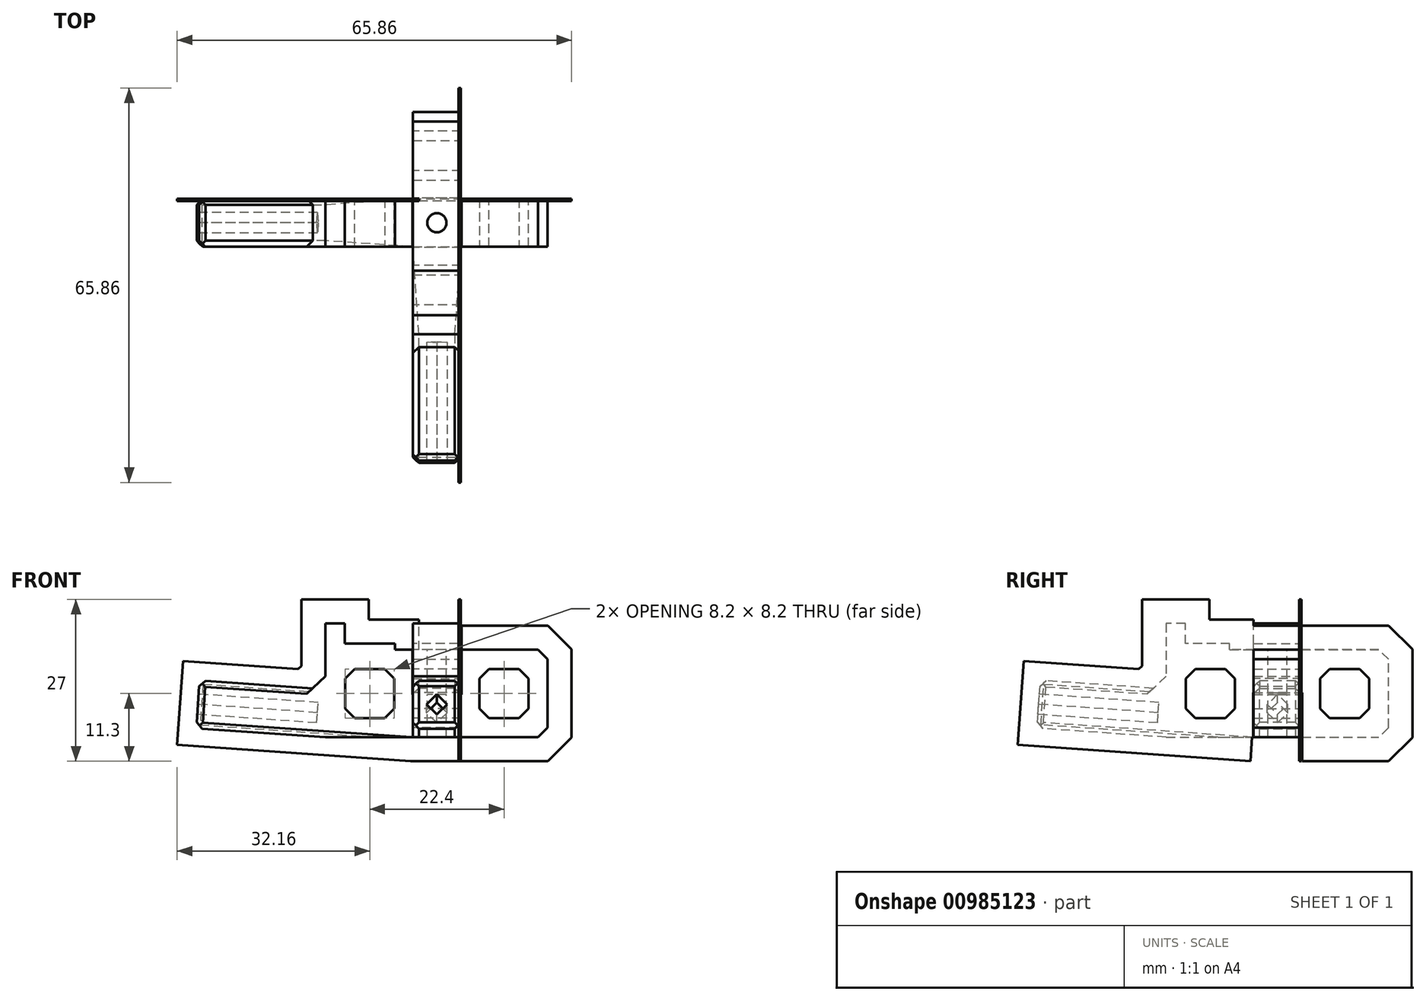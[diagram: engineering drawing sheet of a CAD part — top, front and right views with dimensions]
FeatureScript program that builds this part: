
annotation { "Feature Type Name" : "Feature", "Feature Type Description" : "" }
export const myFeature = defineFeature(function(context is Context, id is Id, definition is map)
    precondition{}
    {
        {
            var Q0;
            Q0=qCreatedBy(makeId("Top.planeOp"),FACE);
            var sketch = newSketch(context, id + "F0", { "sketchPlane" : qUnion([Q0])});
            skLineSegment(sketch, "E0.bottom", {"start": v(0, 0) * mm, "end": v(-5, 0) * mm, "construction": true});
            skLineSegment(sketch, "E0.top", {"start": v(0, -5) * mm, "end": v(-5, -5) * mm, "construction": true});
            skLineSegment(sketch, "E0.left", {"start": v(0, 0) * mm, "end": v(0, -5) * mm, "construction": true});
            skLineSegment(sketch, "E0.right", {"start": v(-5, 0) * mm, "end": v(-5, -5) * mm, "construction": true});
            skLineSegment(sketch, "E1.bottom", {"start": v(0, 0) * mm, "end": v(-15, 0) * mm, "construction": true});
            skLineSegment(sketch, "E1.top", {"start": v(0, -15) * mm, "end": v(-15, -15) * mm, "construction": true});
            skLineSegment(sketch, "E1.left", {"start": v(0, 0) * mm, "end": v(0, -15) * mm, "construction": true});
            skLineSegment(sketch, "E1.right", {"start": v(-15, 0) * mm, "end": v(-15, -15) * mm, "construction": true});
            skCircle(sketch, "E2", {"center": v(0, 0) * mm, "radius": 1.6 * mm, "construction": true});
            skLineSegment(sketch, "E3.bottom", {"start": v(0, 0) * mm, "end": v(-57.4, 0) * mm, "construction": true});
            skLineSegment(sketch, "E3.top", {"start": v(0, -32) * mm, "end": v(-57.4, -32) * mm, "construction": true});
            skLineSegment(sketch, "E3.left", {"start": v(0, 0) * mm, "end": v(0, -32) * mm, "construction": true});
            skLineSegment(sketch, "E3.right", {"start": v(-57.4, 0) * mm, "end": v(-57.4, -32) * mm, "construction": true});
            skSolve(sketch);
        }
        {
            var Q0;
            Q0=qCreatedBy(makeId("Front.planeOp"),FACE);
            var sketch = newSketch(context, id + "F1", { "sketchPlane" : qUnion([Q0])});
            skPoint(sketch, "E4.0", {"position": v(0, 0) * mm});
            skPoint(sketch, "E4.1", {"position": v(-5, 0) * mm});
            skPoint(sketch, "E4.2", {"position": v(-15, 0) * mm});
            skPoint(sketch, "E4.3", {"position": v(-57.4, 0) * mm});
            skLineSegment(sketch, "E5.bottom", {"start": v(0, 0) * mm, "end": v(-57.4, 0) * mm, "construction": true});
            skLineSegment(sketch, "E5.top", {"start": v(0, -2.2) * mm, "end": v(-57.4, -2.2) * mm, "construction": true});
            skLineSegment(sketch, "E5.left", {"start": v(0, 0) * mm, "end": v(0, -2.2) * mm, "construction": true});
            skLineSegment(sketch, "E5.right", {"start": v(-57.4, 0) * mm, "end": v(-57.4, -2.2) * mm, "construction": true});
            skLineSegment(sketch, "E6.bottom", {"start": v(-15, 0) * mm, "end": v(0, 0) * mm, "construction": true});
            skLineSegment(sketch, "E6.top", {"start": v(-15, -8.2) * mm, "end": v(0, -8.2) * mm, "construction": true});
            skLineSegment(sketch, "E6.left", {"start": v(-15, 0) * mm, "end": v(-15, -8.2) * mm, "construction": true});
            skLineSegment(sketch, "E6.right", {"start": v(0, 0) * mm, "end": v(0, -8.2) * mm, "construction": true});
            skLineSegment(sketch, "E7.bottom", {"start": v(-5, 0) * mm, "end": v(0, 0) * mm, "construction": true});
            skLineSegment(sketch, "E7.left", {"start": v(-5, 0) * mm, "end": v(-5, -9.6) * mm, "construction": true});
            skLineSegment(sketch, "E7.right", {"start": v(0, 0) * mm, "end": v(0, -9.6) * mm, "construction": true});
            skLineSegment(sketch, "E8.bottom", {"start": v(-18.6, -9.6) * mm, "end": v(-15.4, -9.6) * mm});
            skLineSegment(sketch, "E8.top", {"start": v(-18.6, -5.2) * mm, "end": v(-15.4, -5.2) * mm});
            skLineSegment(sketch, "E8.left", {"start": v(-18.6, -9.6) * mm, "end": v(-18.6, -5.2) * mm});
            skLineSegment(sketch, "E8.right", {"start": v(-15.4, -9.6) * mm, "end": v(-15.4, -5.2) * mm});
            skLineSegment(sketch, "E9.bottom", {"start": v(0, -24.2) * mm, "end": v(18.5, -24.2) * mm});
            skLineSegment(sketch, "E9.top", {"start": v(0, -9.6) * mm, "end": v(18.5, -9.6) * mm});
            skLineSegment(sketch, "E9.right", {"start": v(18.5, -24.2) * mm, "end": v(18.5, -9.6) * mm});
            skLineSegment(sketch, "E10.left", {"start": v(-18.6, -5.2) * mm, "end": v(-18.6, -11.6) * mm});
            skLineSegment(sketch, "E11.bottom", {"start": v(-15.4, -9.6) * mm, "end": v(-7, -9.6) * mm});
            skLineSegment(sketch, "E11.top", {"start": v(-15.4, -8.6) * mm, "end": v(-7, -8.6) * mm});
            skLineSegment(sketch, "E11.left", {"start": v(-15.4, -9.6) * mm, "end": v(-15.4, -8.6) * mm});
            skLineSegment(sketch, "E11.right", {"start": v(-7, -9.6) * mm, "end": v(-7, -8.6) * mm});
            skLineSegment(sketch, "E12", {"start": v(-18.6, -9.6) * mm, "end": v(-18.6, -24.2) * mm, "construction": true});
            skLineSegment(sketch, "E13", {"start": v(-39.6, -14.71) * mm, "end": v(-18.6, -16.18) * mm});
            skLineSegment(sketch, "E14", {"start": v(-40.16, -22.7) * mm, "end": v(-18.6, -24.2) * mm});
            skLineSegment(sketch, "E15", {"start": v(-39.6, -14.71) * mm, "end": v(-40.16, -22.7) * mm});
            skLineSegment(sketch, "E16", {"start": v(0, -24.2) * mm, "end": v(-18.6, -24.2) * mm});
            skLineSegment(sketch, "E17", {"start": v(-18.6, -9.6) * mm, "end": v(-18.6, -16.18) * mm});
            skLineSegment(sketch, "E18", {"start": v(0, -24.2) * mm, "end": v(0, -9.6) * mm, "construction": true});
            skLineSegment(sketch, "E19", {"start": v(-5, -9.6) * mm, "end": v(0, -9.6) * mm});
            skLineSegment(sketch, "E20", {"start": v(-7, -9.6) * mm, "end": v(-5, -9.6) * mm});
            skLineSegment(sketch, "E21", {"start": v(18.5, -16.9) * mm, "end": v(0, -16.9) * mm, "construction": true});
            skLineSegment(sketch, "E22", {"start": v(0, -16.9) * mm, "end": v(-18.6, -16.9) * mm, "construction": true});
            skLineSegment(sketch, "E23.bottom", {"start": v(-4.1, -9.6) * mm, "end": v(4.1, -9.6) * mm});
            skLineSegment(sketch, "E23.top", {"start": v(-4.1, -17.05) * mm, "end": v(4.1, -17.05) * mm});
            skLineSegment(sketch, "E23.left", {"start": v(-4.1, -9.6) * mm, "end": v(-4.1, -17.05) * mm});
            skLineSegment(sketch, "E23.right", {"start": v(4.1, -9.6) * mm, "end": v(4.1, -17.05) * mm});
            skPoint(sketch, "E23.middle", {"position": v(0, -13.32) * mm});
            skLineSegment(sketch, "E24.bottom", {"start": v(-15.3, -12.8) * mm, "end": v(-7.1, -12.8) * mm});
            skLineSegment(sketch, "E24.top", {"start": v(-15.3, -21) * mm, "end": v(-7.1, -21) * mm});
            skLineSegment(sketch, "E24.left", {"start": v(-15.3, -12.8) * mm, "end": v(-15.3, -21) * mm});
            skLineSegment(sketch, "E24.right", {"start": v(-7.1, -12.8) * mm, "end": v(-7.1, -21) * mm});
            skPoint(sketch, "E24.middle", {"position": v(-11.2, -16.9) * mm});
            skLineSegment(sketch, "E25.bottom", {"start": v(7.1, -12.8) * mm, "end": v(15.3, -12.8) * mm});
            skLineSegment(sketch, "E25.top", {"start": v(7.1, -21) * mm, "end": v(15.3, -21) * mm});
            skLineSegment(sketch, "E25.left", {"start": v(7.1, -12.8) * mm, "end": v(7.1, -21) * mm});
            skLineSegment(sketch, "E25.right", {"start": v(15.3, -12.8) * mm, "end": v(15.3, -21) * mm});
            skPoint(sketch, "E25.middle", {"position": v(11.2, -16.9) * mm});
            skSolve(sketch);
        }
        {
            var Q0;
            Q0=qCreatedBy(makeId("Right.planeOp"),FACE);
            var sketch = newSketch(context, id + "F2", { "sketchPlane" : qUnion([Q0])});
            skPoint(sketch, "E26.0", {"position": v(0, 0) * mm});
            skPoint(sketch, "E26.1", {"position": v(-5, 0) * mm});
            skPoint(sketch, "E26.2", {"position": v(-15, 0) * mm});
            skPoint(sketch, "E26.3", {"position": v(-32, 0) * mm});
            skPoint(sketch, "E27.0", {"position": v(0, -2.2) * mm});
            skPoint(sketch, "E27.1", {"position": v(0, -8.2) * mm});
            skPoint(sketch, "E27.2", {"position": v(0, -9.6) * mm});
            skLineSegment(sketch, "E28.bottom", {"start": v(0, -2.2) * mm, "end": v(-32, -2.2) * mm, "construction": true});
            skLineSegment(sketch, "E28.top", {"start": v(0, 0) * mm, "end": v(-32, 0) * mm, "construction": true});
            skLineSegment(sketch, "E28.left", {"start": v(0, -2.2) * mm, "end": v(0, 0) * mm, "construction": true});
            skLineSegment(sketch, "E28.right", {"start": v(-32, -2.2) * mm, "end": v(-32, 0) * mm, "construction": true});
            skLineSegment(sketch, "E29.bottom", {"start": v(0, -9.6) * mm, "end": v(-5, -9.6) * mm, "construction": true});
            skLineSegment(sketch, "E29.top", {"start": v(0, 0) * mm, "end": v(-5, 0) * mm, "construction": true});
            skLineSegment(sketch, "E29.left", {"start": v(0, -9.6) * mm, "end": v(0, 0) * mm, "construction": true});
            skLineSegment(sketch, "E29.right", {"start": v(-5, -9.6) * mm, "end": v(-5, 0) * mm, "construction": true});
            skLineSegment(sketch, "E30.bottom", {"start": v(0, -8.2) * mm, "end": v(-15, -8.2) * mm, "construction": true});
            skLineSegment(sketch, "E30.top", {"start": v(0, 0) * mm, "end": v(-15, 0) * mm, "construction": true});
            skLineSegment(sketch, "E30.left", {"start": v(0, -8.2) * mm, "end": v(0, 0) * mm, "construction": true});
            skLineSegment(sketch, "E30.right", {"start": v(-15, -8.2) * mm, "end": v(-15, 0) * mm, "construction": true});
            skLineSegment(sketch, "E31.bottom", {"start": v(-15.4, -9.6) * mm, "end": v(-18.6, -9.6) * mm});
            skLineSegment(sketch, "E31.top", {"start": v(-15.4, -5.2) * mm, "end": v(-18.6, -5.2) * mm});
            skLineSegment(sketch, "E31.left", {"start": v(-15.4, -9.6) * mm, "end": v(-15.4, -5.2) * mm});
            skLineSegment(sketch, "E31.right", {"start": v(-18.6, -9.6) * mm, "end": v(-18.6, -5.2) * mm});
            skLineSegment(sketch, "E32.bottom", {"start": v(0, -9.6) * mm, "end": v(18.5, -9.6) * mm});
            skLineSegment(sketch, "E32.top", {"start": v(0, -24.2) * mm, "end": v(18.5, -24.2) * mm});
            skLineSegment(sketch, "E32.left", {"start": v(0, -9.6) * mm, "end": v(0, -24.2) * mm});
            skLineSegment(sketch, "E32.right", {"start": v(18.5, -9.6) * mm, "end": v(18.5, -24.2) * mm});
            skLineSegment(sketch, "E33.left", {"start": v(-18.6, -5.2) * mm, "end": v(-18.6, -9.8) * mm});
            skLineSegment(sketch, "E34.bottom", {"start": v(-15.4, -9.6) * mm, "end": v(-8, -9.6) * mm});
            skLineSegment(sketch, "E34.top", {"start": v(-15.4, -8.6) * mm, "end": v(-8, -8.6) * mm});
            skLineSegment(sketch, "E34.left", {"start": v(-15.4, -9.6) * mm, "end": v(-15.4, -8.6) * mm});
            skLineSegment(sketch, "E34.right", {"start": v(-8, -9.6) * mm, "end": v(-8, -8.6) * mm});
            skLineSegment(sketch, "E35", {"start": v(18.5, -16.9) * mm, "end": v(-11.2, -16.9) * mm, "construction": true});
            skLineSegment(sketch, "E36.bottom", {"start": v(-4.1, -24.2) * mm, "end": v(4.1, -24.2) * mm});
            skLineSegment(sketch, "E36.top", {"start": v(-4.1, -16.75) * mm, "end": v(4.1, -16.75) * mm});
            skLineSegment(sketch, "E36.left", {"start": v(-4.1, -24.2) * mm, "end": v(-4.1, -16.75) * mm});
            skLineSegment(sketch, "E36.right", {"start": v(4.1, -24.2) * mm, "end": v(4.1, -16.75) * mm});
            skPoint(sketch, "E36.middle", {"position": v(0, -20.48) * mm});
            skLineSegment(sketch, "E37", {"start": v(-8, -9.6) * mm, "end": v(0, -9.6) * mm});
            skLineSegment(sketch, "E38", {"start": v(-15.4, -9.6) * mm, "end": v(-15.4, -24.2) * mm, "construction": true});
            skLineSegment(sketch, "E39", {"start": v(-15.4, -24.2) * mm, "end": v(-15.4, -24.2) * mm});
            skLineSegment(sketch, "E40", {"start": v(-15.4, -24.2) * mm, "end": v(-4.1, -24.2) * mm});
            skLineSegment(sketch, "E41", {"start": v(-11.2, -16.9) * mm, "end": v(-15.4, -16.9) * mm, "construction": true});
            skLineSegment(sketch, "E42.bottom", {"start": v(-15.3, -12.8) * mm, "end": v(-7.1, -12.8) * mm});
            skLineSegment(sketch, "E42.top", {"start": v(-15.3, -21) * mm, "end": v(-7.1, -21) * mm});
            skLineSegment(sketch, "E42.left", {"start": v(-15.3, -12.8) * mm, "end": v(-15.3, -21) * mm});
            skLineSegment(sketch, "E42.right", {"start": v(-7.1, -12.8) * mm, "end": v(-7.1, -21) * mm});
            skPoint(sketch, "E42.middle", {"position": v(-11.2, -16.9) * mm});
            skLineSegment(sketch, "E43.bottom", {"start": v(7.1, -12.8) * mm, "end": v(15.3, -12.8) * mm});
            skLineSegment(sketch, "E43.top", {"start": v(7.1, -21) * mm, "end": v(15.3, -21) * mm});
            skLineSegment(sketch, "E43.left", {"start": v(7.1, -12.8) * mm, "end": v(7.1, -21) * mm});
            skLineSegment(sketch, "E43.right", {"start": v(15.3, -12.8) * mm, "end": v(15.3, -21) * mm});
            skPoint(sketch, "E43.middle", {"position": v(11.2, -16.9) * mm});
            skLineSegment(sketch, "E44", {"start": v(-39.6, -14.71) * mm, "end": v(-18.6, -16.18) * mm});
            skLineSegment(sketch, "E45", {"start": v(-40.16, -22.7) * mm, "end": v(-39.6, -14.71) * mm});
            skLineSegment(sketch, "E46", {"start": v(-18.6, -24.2) * mm, "end": v(-40.16, -22.7) * mm});
            skLineSegment(sketch, "E47", {"start": v(-15.4, -24.2) * mm, "end": v(-18.6, -24.2) * mm});
            skLineSegment(sketch, "E48", {"start": v(-18.6, -9.6) * mm, "end": v(-18.6, -16.18) * mm});
            skLineSegment(sketch, "E49", {"start": v(-18.6, -9.6) * mm, "end": v(-18.6, -24.2) * mm, "construction": true});
            skPoint(sketch, "E50.0", {"position": v(0, -24.2) * mm});
            skSolve(sketch);
        }
        {
            var Q0;
            Q0=makeQuery(id+"F2.imprint","IMPRINT",FACE,{"disambiguationData":[TD([[makeQuery(id+"F2.imprint","IMPRINT",EDGE,{"derivedFrom":sQuery(id+"F2.wireOp",EDGE,"E31.bottom")}),-1.0]])]});
            var Q1;
            Q1=makeQuery(id+"F2.imprint","IMPRINT",FACE,{"disambiguationData":[TD([[makeQuery(id+"F2.imprint","IMPRINT",EDGE,{"derivedFrom":sQuery(id+"F2.wireOp",EDGE,"E32.bottom")}),-1.0]])]});
            var Q2;
            {var subQ4=sQuery(id+"F2.wireOp",EDGE,"OBChvoAJ-RbBw-G4Zu-pUpg-qMR8gtXd1GRA.bottom");Q2=makeQuery(id+"F2.imprint","IMPRINT",FACE,{"disambiguationData":[TD([[makeQuery(id+"F2.imprint","IMPRINT",EDGE,{"derivedFrom":subQ4}),-1.0]])]});}
            var Q3;
            {var subQ2=sQuery(id+"F2.wireOp",EDGE,"8gTq5QkP-tqKR-gVNM-ihy2-sNKQO3E6GvEK.bottom");Q3=makeQuery(id+"F2.imprint","IMPRINT",FACE,{"disambiguationData":[TD([[makeQuery(id+"F2.imprint","IMPRINT",EDGE,{"derivedFrom":subQ2}),-1.0]])]});}
            var Q4;
            {var subQ5=sQuery(id+"F2.wireOp",EDGE,"JYyk69A0-JFX6-SWJj-MqIX-1RuSluLhbpVE");Q4=makeQuery(id+"F2.imprint","IMPRINT",FACE,{"disambiguationData":[TD([[makeQuery(id+"F2.imprint","IMPRINT",EDGE,{"derivedFrom":subQ5}),-1.0]])]});}
            var Q5;
            {var subQ0=sQuery(id+"F2.wireOp",EDGE,"E31.bottom");Q5=makeQuery(id+"F2.imprint","IMPRINT",FACE,{"disambiguationData":[TD([[makeQuery(id+"F2.imprint","IMPRINT",EDGE,{"derivedFrom":subQ0}),1.0]])]});}
            var Q6;
            {var subQ0=sQuery(id+"F2.wireOp",EDGE,"BySTftVg-rPwj-K5M3-Ot8g-HlblG6s6wdVx.bottom");var subQ1=sQuery(id+"F2.wireOp",EDGE,"8gTq5QkP-tqKR-gVNM-ihy2-sNKQO3E6GvEK.left");var subQ2=makeQuery(id+"F2.imprint","INTERSECT",VERTEX,{"derivedFrom":[subQ1,subQ0]});Q6=makeQuery(id+"F2.imprint","IMPRINT",FACE,{"disambiguationData":[TD([[makeQuery(id+"F2.imprint","IMPRINT",EDGE,{"disambiguationData":[TD([[subQ2,-1.0]])],"derivedFrom":subQ1}),1.0]])]});}
            var Q7;
            {var subQ0=sQuery(id+"F2.wireOp",EDGE,"BySTftVg-rPwj-K5M3-Ot8g-HlblG6s6wdVx.bottom");var subQ1=sQuery(id+"F2.wireOp",EDGE,"8gTq5QkP-tqKR-gVNM-ihy2-sNKQO3E6GvEK.left");var subQ2=makeQuery(id+"F2.imprint","INTERSECT",VERTEX,{"derivedFrom":[subQ1,subQ0]});Q7=makeQuery(id+"F2.imprint","IMPRINT",FACE,{"disambiguationData":[TD([[makeQuery(id+"F2.imprint","IMPRINT",EDGE,{"disambiguationData":[TD([[subQ2,-1.0]])],"derivedFrom":subQ1}),-1.0]])]});}
            var Q8;
            {var subQ5=sQuery(id+"F2.wireOp",EDGE,"VJ3Hrh6b-9nXv-4qbG-uLe8-7kU1UBrJx5E7.top");Q8=makeQuery(id+"F2.imprint","IMPRINT",FACE,{"disambiguationData":[TD([[makeQuery(id+"F2.imprint","IMPRINT",EDGE,{"derivedFrom":subQ5}),1.0]])]});}
            var Q9;
            {var subQ0=sQuery(id+"F2.wireOp",EDGE,"TiXIGDB8-BmQa-Wkej-lV4T-48hGmIpaURQ9");Q9=makeQuery(id+"F2.imprint","IMPRINT",FACE,{"disambiguationData":[TD([[makeQuery(id+"F2.imprint","IMPRINT",EDGE,{"derivedFrom":subQ0}),-1.0]])]});}
            var Q10;
            {var subQ5=sQuery(id+"F2.wireOp",EDGE,"VJ3Hrh6b-9nXv-4qbG-uLe8-7kU1UBrJx5E7.bottom");Q10=makeQuery(id+"F2.imprint","IMPRINT",FACE,{"disambiguationData":[TD([[makeQuery(id+"F2.imprint","IMPRINT",EDGE,{"derivedFrom":subQ5}),-1.0]])]});}
            var Q11;
            {var subQ10=sQuery(id+"F2.wireOp",EDGE,"E33.right");Q11=makeQuery(id+"F2.imprint","IMPRINT",FACE,{"disambiguationData":[TD([[makeQuery(id+"F2.imprint","IMPRINT",EDGE,{"derivedFrom":subQ10}),-1.0]])]});}
            var Q12;
            Q12=makeQuery(id+"F2.imprint","IMPRINT",FACE,{"disambiguationData":[TD([[makeQuery(id+"F2.imprint","IMPRINT",EDGE,{"derivedFrom":sQuery(id+"F2.wireOp",EDGE,"E34.bottom")}),1.0]])]});
            var Q13;
            {var subQ0=sQuery(id+"F2.wireOp",EDGE,"BySTftVg-rPwj-K5M3-Ot8g-HlblG6s6wdVx.bottom");var subQ1=sQuery(id+"F2.wireOp",EDGE,"OBChvoAJ-RbBw-G4Zu-pUpg-qMR8gtXd1GRA.right");var subQ2=makeQuery(id+"F2.imprint","INTERSECT",VERTEX,{"derivedFrom":[subQ1,subQ0]});Q13=makeQuery(id+"F2.imprint","IMPRINT",FACE,{"disambiguationData":[TD([[makeQuery(id+"F2.imprint","IMPRINT",EDGE,{"disambiguationData":[TD([[subQ2,-1.0]])],"derivedFrom":subQ1}),-1.0]])]});}
            var Q14;
            Q14=makeQuery(id+"F4.opExtrude","SWEPT_FACE",FACE,{"disambiguationData":[OSD([sQuery(id+"F1.wireOp",EDGE,"CqF1PMtX-XOxb-3WgB-e5Ex-kUzRkycBYxmF.top"),sQuery(id+"F1.wireOp",EDGE,"E9.bottom")])]});
            var Q15;
            {var subQ0=sQuery(id+"F2.wireOp",EDGE,"QTA5FS13-UDDy-iq4O-vZLj-EMgIGIXr1umF");Q15=makeQuery(id+"F2.imprint","IMPRINT",FACE,{"disambiguationData":[TD([[makeQuery(id+"F2.imprint","IMPRINT",EDGE,{"derivedFrom":subQ0}),1.0]])]});}
            var Q16;
            {var subQ4=sQuery(id+"F2.wireOp",EDGE,"E39");Q16=makeQuery(id+"F2.imprint","IMPRINT",FACE,{"disambiguationData":[TD([[makeQuery(id+"F2.imprint","IMPRINT",EDGE,{"derivedFrom":subQ4}),-1.0]])]});}
            var Q17;
            {var subQ0=sQuery(id+"F2.wireOp",EDGE,"fbhIcDKn-QlwI-lRDL-BWJN-GHHaVk2E9Y9V");var subQ1=sQuery(id+"F2.wireOp",EDGE,"E36.right");var subQ2=makeQuery(id+"F2.imprint","INTERSECT",VERTEX,{"derivedFrom":[subQ1,subQ0]});Q17=makeQuery(id+"F2.imprint","IMPRINT",FACE,{"disambiguationData":[TD([[makeQuery(id+"F2.imprint","IMPRINT",EDGE,{"disambiguationData":[TD([[subQ2,-1.0]])],"derivedFrom":subQ1}),-1.0]])]});}
            var Q18;
            {var subQ0=sQuery(id+"F2.wireOp",EDGE,"E44");Q18=makeQuery(id+"F2.imprint","IMPRINT",FACE,{"disambiguationData":[TD([[makeQuery(id+"F2.imprint","IMPRINT",EDGE,{"derivedFrom":subQ0}),-1.0]])]});}
            extrude(context, id + "F3", {"entities" : qUnion([Q0, Q1, Q2, Q3, Q4, Q5, Q6, Q7, Q8, Q9, Q10, Q11, Q12, Q13, Q14, Q15, Q16, Q17, Q18]), "depth" : 8 * mm, "offsetDistance" : 25 * mm, "symmetric" : true});
        }
        {
            var Q0;
            Q0=makeQuery(id+"F1.imprint","IMPRINT",FACE,{"disambiguationData":[TD([[makeQuery(id+"F1.imprint","IMPRINT",EDGE,{"derivedFrom":sQuery(id+"F1.wireOp",EDGE,"E8.bottom")}),1.0]])]});
            var Q1;
            Q1=makeQuery(id+"F1.imprint","IMPRINT",FACE,{"disambiguationData":[TD([[makeQuery(id+"F1.imprint","IMPRINT",EDGE,{"derivedFrom":sQuery(id+"F1.wireOp",EDGE,"E9.bottom")}),1.0]])]});
            var Q2;
            {var subQ2=sQuery(id+"F1.wireOp",EDGE,"jBLO5fWm-ZUce-OGYA-eWwh-CTL6BHp59DrC.bottom");Q2=makeQuery(id+"F1.imprint","IMPRINT",FACE,{"disambiguationData":[TD([[makeQuery(id+"F1.imprint","IMPRINT",EDGE,{"derivedFrom":subQ2}),-1.0]])]});}
            var Q3;
            {var subQ1=sQuery(id+"F1.wireOp",EDGE,"X2ukl4HH-mULt-C7Bp-0cCv-Kh8miEkw12V0");Q3=makeQuery(id+"F1.imprint","IMPRINT",FACE,{"disambiguationData":[TD([[makeQuery(id+"F1.imprint","IMPRINT",EDGE,{"derivedFrom":subQ1}),-1.0]])]});}
            var Q4;
            {var subQ0=sQuery(id+"F1.wireOp",EDGE,"E8.bottom");Q4=makeQuery(id+"F1.imprint","IMPRINT",FACE,{"disambiguationData":[TD([[makeQuery(id+"F1.imprint","IMPRINT",EDGE,{"derivedFrom":subQ0}),-1.0]])]});}
            var Q5;
            {var subQ0=sQuery(id+"F1.wireOp",EDGE,"E9.top");Q5=makeQuery(id+"F1.imprint","IMPRINT",FACE,{"disambiguationData":[TD([[makeQuery(id+"F1.imprint","IMPRINT",EDGE,{"derivedFrom":subQ0}),-1.0]])]});}
            var Q6;
            {var subQ0=sQuery(id+"F1.wireOp",EDGE,"8lrkMEmI-apU0-wW4B-mjhf-344KdWqfUMjU.bottom");var subQ1=sQuery(id+"F1.wireOp",EDGE,"jBLO5fWm-ZUce-OGYA-eWwh-CTL6BHp59DrC.left");var subQ2=makeQuery(id+"F1.imprint","INTERSECT",VERTEX,{"derivedFrom":[subQ1,subQ0]});Q6=makeQuery(id+"F1.imprint","IMPRINT",FACE,{"disambiguationData":[TD([[makeQuery(id+"F1.imprint","IMPRINT",EDGE,{"disambiguationData":[TD([[subQ2,-1.0]])],"derivedFrom":subQ1}),1.0]])]});}
            var Q7;
            {var subQ0=sQuery(id+"F1.wireOp",EDGE,"8lrkMEmI-apU0-wW4B-mjhf-344KdWqfUMjU.bottom");var subQ1=sQuery(id+"F1.wireOp",EDGE,"jBLO5fWm-ZUce-OGYA-eWwh-CTL6BHp59DrC.left");var subQ2=makeQuery(id+"F1.imprint","INTERSECT",VERTEX,{"derivedFrom":[subQ1,subQ0]});Q7=makeQuery(id+"F1.imprint","IMPRINT",FACE,{"disambiguationData":[TD([[makeQuery(id+"F1.imprint","IMPRINT",EDGE,{"disambiguationData":[TD([[subQ2,-1.0]])],"derivedFrom":subQ1}),-1.0]])]});}
            var Q8;
            {var subQ5=sQuery(id+"F1.wireOp",EDGE,"G9mchs2O-4KQI-hap8-ZQsE-f4JrX58Ms06i.top");Q8=makeQuery(id+"F1.imprint","IMPRINT",FACE,{"disambiguationData":[TD([[makeQuery(id+"F1.imprint","IMPRINT",EDGE,{"derivedFrom":subQ5}),1.0]])]});}
            var Q9;
            {var subQ5=sQuery(id+"F1.wireOp",EDGE,"G9mchs2O-4KQI-hap8-ZQsE-f4JrX58Ms06i.bottom");Q9=makeQuery(id+"F1.imprint","IMPRINT",FACE,{"disambiguationData":[TD([[makeQuery(id+"F1.imprint","IMPRINT",EDGE,{"derivedFrom":subQ5}),-1.0]])]});}
            var Q10;
            {var subQ0=sQuery(id+"F1.wireOp",EDGE,"88LbmJ9p-CLms-JCYk-9GDK-1dHX8rH5Mll8");Q10=makeQuery(id+"F1.imprint","IMPRINT",FACE,{"disambiguationData":[TD([[makeQuery(id+"F1.imprint","IMPRINT",EDGE,{"derivedFrom":subQ0}),-1.0]])]});}
            var Q11;
            {var subQ8=sQuery(id+"F1.wireOp",EDGE,"E10.right");Q11=makeQuery(id+"F1.imprint","IMPRINT",FACE,{"disambiguationData":[TD([[makeQuery(id+"F1.imprint","IMPRINT",EDGE,{"derivedFrom":subQ8}),-1.0]])]});}
            var Q12;
            Q12=makeQuery(id+"F1.imprint","IMPRINT",FACE,{"disambiguationData":[TD([[makeQuery(id+"F1.imprint","IMPRINT",EDGE,{"derivedFrom":sQuery(id+"F1.wireOp",EDGE,"E11.bottom")}),1.0]])]});
            var Q13;
            {var subQ1=sQuery(id+"F1.wireOp",EDGE,"6YMqiNCV-82d4-Ad4x-QHJ8-AYQC3T5fh0Wm");var subQ5=sQuery(id+"F1.wireOp",EDGE,"8lrkMEmI-apU0-wW4B-mjhf-344KdWqfUMjU.top");var subQ6=makeQuery(id+"F1.imprint","INTERSECT",VERTEX,{"derivedFrom":[subQ5,subQ1]});Q13=makeQuery(id+"F1.imprint","IMPRINT",FACE,{"disambiguationData":[TD([[makeQuery(id+"F1.imprint","IMPRINT",EDGE,{"disambiguationData":[TD([[subQ6,-1.0]])],"derivedFrom":subQ5}),1.0]])]});}
            var Q14;
            {var subQ0=sQuery(id+"F1.wireOp",EDGE,"EttqwHYU-FuiR-qyt9-x16j-VCJwsENre23n");Q14=makeQuery(id+"F1.imprint","IMPRINT",FACE,{"disambiguationData":[TD([[makeQuery(id+"F1.imprint","IMPRINT",EDGE,{"derivedFrom":subQ0}),-1.0]])]});}
            var Q15;
            {var subQ0=sQuery(id+"F1.wireOp",EDGE,"6YMqiNCV-82d4-Ad4x-QHJ8-AYQC3T5fh0Wm");var subQ1=sQuery(id+"F1.wireOp",EDGE,"8lrkMEmI-apU0-wW4B-mjhf-344KdWqfUMjU.top");var subQ2=makeQuery(id+"F1.imprint","INTERSECT",VERTEX,{"derivedFrom":[subQ1,subQ0]});Q15=makeQuery(id+"F1.imprint","IMPRINT",FACE,{"disambiguationData":[TD([[makeQuery(id+"F1.imprint","IMPRINT",EDGE,{"disambiguationData":[TD([[subQ2,-1.0]])],"derivedFrom":subQ1}),-1.0]])]});}
            var Q16;
            {var subQ0=sQuery(id+"F1.wireOp",EDGE,"VmZ0w6UW-0Vx5-MZEa-9MV1-IjLl1K2J6mHU");Q16=makeQuery(id+"F1.imprint","IMPRINT",FACE,{"disambiguationData":[TD([[makeQuery(id+"F1.imprint","IMPRINT",EDGE,{"derivedFrom":subQ0}),-1.0]])]});}
            var Q17;
            {var subQ7=sQuery(id+"F1.wireOp",EDGE,"kZNcDHxd-jaCr-3rhE-A8Yc-3WcHj5bUUv40");Q17=makeQuery(id+"F1.imprint","IMPRINT",FACE,{"disambiguationData":[TD([[makeQuery(id+"F1.imprint","IMPRINT",EDGE,{"derivedFrom":subQ7}),-1.0]])]});}
            extrude(context, id + "F4", {"entities" : qUnion([Q0, Q1, Q2, Q3, Q4, Q5, Q6, Q7, Q8, Q9, Q10, Q11, Q12, Q13, Q14, Q15, Q16, Q17]), "depth" : 8 * mm, "offsetDistance" : 25 * mm, "symmetric" : true});
        }
        {
            var Q0;
            Q0=makeQuery(id+"F4.opExtrude","SWEPT_FACE",FACE,{"disambiguationData":[OSD([sQuery(id+"F1.wireOp",EDGE,"E15")])]});
            var sketch = newSketch(context, id + "F5", { "sketchPlane" : qUnion([Q0])});
            skLineSegment(sketch, "E51", {"start": v(0, -17.44) * mm, "end": v(0, -25.44) * mm, "construction": true});
            skLineSegment(sketch, "E52", {"start": v(-4, -21.44) * mm, "end": v(4, -21.44) * mm, "construction": true});
            skCircle(sketch, "E53", {"center": v(0, -21.44) * mm, "radius": 1.7 * mm, "construction": true});
            skLineSegment(sketch, "E54", {"start": v(-1.7, -21.44) * mm, "end": v(0, -19.74) * mm});
            skLineSegment(sketch, "E55", {"start": v(0, -19.74) * mm, "end": v(1.7, -21.44) * mm});
            skLineSegment(sketch, "E56", {"start": v(1.7, -21.44) * mm, "end": v(0, -23.14) * mm});
            skLineSegment(sketch, "E57", {"start": v(0, -23.14) * mm, "end": v(-1.7, -21.44) * mm});
            skSolve(sketch);
        }
        {
            var Q0;
            Q0=qSketchRegion(id+"F5",true);
            var Q1;
            {var subQ0=sQuery(id+"F5.wireOp",EDGE,"DmRUD49h-oOMy-aDUF-b3qi-gqbV5ypZ8UCy");Q1=makeQuery(id+"F5.imprint","IMPRINT",FACE,{"disambiguationData":[TD([[makeQuery(id+"F5.imprint","IMPRINT",EDGE,{"derivedFrom":subQ0}),1.0]])]});}
            var Q2;
            {var subQ0=sQuery(id+"F5.wireOp",EDGE,"gyTJ5oP8-qJG5-twmr-K78g-cio2S3BSXBqK");Q2=makeQuery(id+"F5.imprint","IMPRINT",FACE,{"disambiguationData":[TD([[makeQuery(id+"F5.imprint","IMPRINT",EDGE,{"derivedFrom":subQ0}),1.0]])]});}
            var Q3;
            {var subQ0=sQuery(id+"F5.wireOp",EDGE,"hhUynoNL-uImP-Ygfq-kCPe-bANWSFwAqyqV");Q3=makeQuery(id+"F5.imprint","IMPRINT",FACE,{"disambiguationData":[TD([[makeQuery(id+"F5.imprint","IMPRINT",EDGE,{"derivedFrom":subQ0}),-1.0]])]});}
            var Q4;
            {var subQ0=sQuery(id+"F5.wireOp",EDGE,"VEbs3MT7-Y1Mt-c6mR-xf3E-mZXncg7GQQ4D");Q4=makeQuery(id+"F5.imprint","IMPRINT",FACE,{"disambiguationData":[TD([[makeQuery(id+"F5.imprint","IMPRINT",EDGE,{"derivedFrom":subQ0}),-1.0]])]});}
            var Q5;
            {var subQ0=sQuery(id+"F5.wireOp",EDGE,"4V46c4tC-SSp1-gxpJ-iT8X-aYr1PGVHphDc");Q5=makeQuery(id+"F5.imprint","IMPRINT",FACE,{"disambiguationData":[TD([[makeQuery(id+"F5.imprint","IMPRINT",EDGE,{"derivedFrom":subQ0}),-1.0]])]});}
            var Q6;
            {var subQ0=sQuery(id+"F5.wireOp",EDGE,"GAJuuTYb-7CHK-ZLYu-xZtS-Suc8JZjJQdwZ");Q6=makeQuery(id+"F5.imprint","IMPRINT",FACE,{"disambiguationData":[TD([[makeQuery(id+"F5.imprint","IMPRINT",EDGE,{"derivedFrom":subQ0}),1.0]])]});}
            extrude(context, id + "F6", {"entities" : qUnion([Q0, Q1, Q2, Q3, Q4, Q5, Q6]), "operationType" : NewBodyOperationType.REMOVE, "oppositeDirection" : true, "depth" : 20 * mm, "offsetDistance" : 25 * mm});
        }
        {
            var Q0;
            Q0=makeQuery(id+"F3.opExtrude","SWEPT_FACE",FACE,{"disambiguationData":[OSD([sQuery(id+"F2.wireOp",EDGE,"E45")])]});
            var sketch = newSketch(context, id + "F7", { "sketchPlane" : qUnion([Q0])});
            skLineSegment(sketch, "E58", {"start": v(-4, -21.44) * mm, "end": v(4, -21.44) * mm, "construction": true});
            skLineSegment(sketch, "E59", {"start": v(0, -17.44) * mm, "end": v(0, -25.44) * mm, "construction": true});
            skCircle(sketch, "E60", {"center": v(0, -21.44) * mm, "radius": 1.7 * mm, "construction": true});
            skLineSegment(sketch, "E61", {"start": v(-1.7, -21.44) * mm, "end": v(0, -19.74) * mm});
            skLineSegment(sketch, "E62", {"start": v(0, -19.74) * mm, "end": v(1.7, -21.44) * mm});
            skLineSegment(sketch, "E63", {"start": v(1.7, -21.44) * mm, "end": v(0, -23.14) * mm});
            skLineSegment(sketch, "E64", {"start": v(0, -23.14) * mm, "end": v(-1.7, -21.44) * mm});
            skSolve(sketch);
        }
        {
            var Q0;
            Q0=makeQuery(id+"F7.imprint","IMPRINT",FACE,{"disambiguationData":[TD([[makeQuery(id+"F7.imprint","IMPRINT",EDGE,{"derivedFrom":sQuery(id+"F7.wireOp",EDGE,"E61")}),-1.0]])]});
            extrude(context, id + "F8", {"entities" : qUnion([Q0]), "operationType" : NewBodyOperationType.REMOVE, "oppositeDirection" : true, "depth" : 20 * mm, "offsetDistance" : 25 * mm});
        }
        {
            var Q0;
            Q0=makeQuery(id+"F3.opExtrude","SWEPT_FACE",FACE,{"disambiguationData":[OSD([sQuery(id+"F2.wireOp",EDGE,"E32.bottom"),sQuery(id+"F2.wireOp",EDGE,"E37")])]});
            var sketch = newSketch(context, id + "F9", { "sketchPlane" : qUnion([Q0])});
            skCircle(sketch, "E65.0", {"center": v(0, 0) * mm, "radius": 1.6 * mm});
            skSolve(sketch);
        }
        {
            var Q0;
            Q0=makeQuery(id+"F9.imprint","IMPRINT",FACE,{"disambiguationData":[TD([[makeQuery(id+"F9.imprint","IMPRINT",EDGE,{"derivedFrom":sQuery(id+"F9.wireOp",EDGE,"E65.0")}),1.0]])]});
            extrude(context, id + "F10", {"entities" : qUnion([Q0]), "operationType" : NewBodyOperationType.REMOVE, "oppositeDirection" : true, "depth" : 25 * mm, "offsetDistance" : 25 * mm});
        }
        {
            var Q0;
            Q0=makeQuery(id+"F3.opExtrude","SWEPT_EDGE",EDGE,{"disambiguationData":[OSD([sQuery(id+"F2.wireOp",EDGE,"E44"),sQuery(id+"F2.wireOp",EDGE,"E48")])]});
            var Q1;
            Q1=makeQuery(id+"F4.opExtrude","SWEPT_EDGE",EDGE,{"disambiguationData":[OSD([sQuery(id+"F1.wireOp",EDGE,"E13"),sQuery(id+"F1.wireOp",EDGE,"E17")])]});
            chamfer(context, id + "F11", {"entities" : qUnion([Q0, Q1]), "width" : 2 * mm, "tangentPropagation" : true});
        }
        {
            var Q0;
            Q0=makeQuery(id+"F4.opExtrude","SWEPT_EDGE",EDGE,{"disambiguationData":[OSD([sQuery(id+"F1.wireOp",EDGE,"E9.top"),sQuery(id+"F1.wireOp",EDGE,"E9.right")])]});
            var Q1;
            Q1=makeQuery(id+"F4.opExtrude","SWEPT_EDGE",EDGE,{"disambiguationData":[OSD([sQuery(id+"F1.wireOp",EDGE,"E9.bottom"),sQuery(id+"F1.wireOp",EDGE,"E9.right")])]});
            var Q2;
            Q2=makeQuery(id+"F3.opExtrude","SWEPT_EDGE",EDGE,{"disambiguationData":[OSD([sQuery(id+"F2.wireOp",EDGE,"E32.top"),sQuery(id+"F2.wireOp",EDGE,"E32.right")])]});
            var Q3;
            Q3=makeQuery(id+"F3.opExtrude","SWEPT_EDGE",EDGE,{"disambiguationData":[OSD([sQuery(id+"F2.wireOp",EDGE,"E32.bottom"),sQuery(id+"F2.wireOp",EDGE,"E32.right")])]});
            var Q4;
            Q4=makeQuery(id+"F4.opExtrude","SWEPT_EDGE",EDGE,{"disambiguationData":[OSD([sQuery(id+"F1.wireOp",EDGE,"CqF1PMtX-XOxb-3WgB-e5Ex-kUzRkycBYxmF.top"),sQuery(id+"F1.wireOp",EDGE,"kZNcDHxd-jaCr-3rhE-A8Yc-3WcHj5bUUv40")])]});
            chamfer(context, id + "F12", {"entities" : qUnion([Q0, Q1, Q2, Q3, Q4]), "width" : 1.6 * mm, "tangentPropagation" : true});
        }
        {
            var Q0;
            Q0=makeQuery(id+"F4.opExtrude","SWEPT_EDGE",EDGE,{"disambiguationData":[OSD([sQuery(id+"F1.wireOp",EDGE,"JE9xJt7m-wwiV-eNkO-kHE2-m3JgbCnZkmdB.bottom"),sQuery(id+"F1.wireOp",EDGE,"JE9xJt7m-wwiV-eNkO-kHE2-m3JgbCnZkmdB.left")])]});
            var Q1;
            Q1=makeQuery(id+"F4.opExtrude","SWEPT_EDGE",EDGE,{"disambiguationData":[OSD([sQuery(id+"F1.wireOp",EDGE,"JE9xJt7m-wwiV-eNkO-kHE2-m3JgbCnZkmdB.bottom"),sQuery(id+"F1.wireOp",EDGE,"JE9xJt7m-wwiV-eNkO-kHE2-m3JgbCnZkmdB.right")])]});
            var Q2;
            Q2=makeQuery(id+"F4.opExtrude","SWEPT_EDGE",EDGE,{"disambiguationData":[OSD([sQuery(id+"F1.wireOp",EDGE,"JE9xJt7m-wwiV-eNkO-kHE2-m3JgbCnZkmdB.top"),sQuery(id+"F1.wireOp",EDGE,"JE9xJt7m-wwiV-eNkO-kHE2-m3JgbCnZkmdB.right")])]});
            var Q3;
            Q3=makeQuery(id+"F4.opExtrude","SWEPT_EDGE",EDGE,{"disambiguationData":[OSD([sQuery(id+"F1.wireOp",EDGE,"JE9xJt7m-wwiV-eNkO-kHE2-m3JgbCnZkmdB.top"),sQuery(id+"F1.wireOp",EDGE,"JE9xJt7m-wwiV-eNkO-kHE2-m3JgbCnZkmdB.left")])]});
            var Q4;
            Q4=makeQuery(id+"F4.opExtrude","SWEPT_EDGE",EDGE,{"disambiguationData":[OSD([sQuery(id+"F1.wireOp",EDGE,"p52yJi1s-9XlR-7mdP-Lo16-mDpjl8GKw8hE.top"),sQuery(id+"F1.wireOp",EDGE,"p52yJi1s-9XlR-7mdP-Lo16-mDpjl8GKw8hE.left")])]});
            var Q5;
            Q5=makeQuery(id+"F4.opExtrude","SWEPT_EDGE",EDGE,{"disambiguationData":[OSD([sQuery(id+"F1.wireOp",EDGE,"p52yJi1s-9XlR-7mdP-Lo16-mDpjl8GKw8hE.bottom"),sQuery(id+"F1.wireOp",EDGE,"p52yJi1s-9XlR-7mdP-Lo16-mDpjl8GKw8hE.left")])]});
            var Q6;
            Q6=makeQuery(id+"F4.opExtrude","SWEPT_EDGE",EDGE,{"disambiguationData":[OSD([sQuery(id+"F1.wireOp",EDGE,"p52yJi1s-9XlR-7mdP-Lo16-mDpjl8GKw8hE.bottom"),sQuery(id+"F1.wireOp",EDGE,"p52yJi1s-9XlR-7mdP-Lo16-mDpjl8GKw8hE.right")])]});
            var Q7;
            Q7=makeQuery(id+"F4.opExtrude","SWEPT_EDGE",EDGE,{"disambiguationData":[OSD([sQuery(id+"F1.wireOp",EDGE,"p52yJi1s-9XlR-7mdP-Lo16-mDpjl8GKw8hE.top"),sQuery(id+"F1.wireOp",EDGE,"p52yJi1s-9XlR-7mdP-Lo16-mDpjl8GKw8hE.right")])]});
            var Q8;
            Q8=makeQuery(id+"F3.opExtrude","SWEPT_EDGE",EDGE,{"disambiguationData":[OSD([sQuery(id+"F2.wireOp",EDGE,"E42.bottom"),sQuery(id+"F2.wireOp",EDGE,"E42.right")])]});
            var Q9;
            Q9=makeQuery(id+"F3.opExtrude","SWEPT_EDGE",EDGE,{"disambiguationData":[OSD([sQuery(id+"F2.wireOp",EDGE,"E43.bottom"),sQuery(id+"F2.wireOp",EDGE,"E43.right")])]});
            var Q10;
            Q10=makeQuery(id+"F3.opExtrude","SWEPT_EDGE",EDGE,{"disambiguationData":[OSD([sQuery(id+"F2.wireOp",EDGE,"E42.bottom"),sQuery(id+"F2.wireOp",EDGE,"E42.left")])]});
            var Q11;
            Q11=makeQuery(id+"F3.opExtrude","SWEPT_EDGE",EDGE,{"disambiguationData":[OSD([sQuery(id+"F2.wireOp",EDGE,"E42.top"),sQuery(id+"F2.wireOp",EDGE,"E42.right")])]});
            var Q12;
            Q12=makeQuery(id+"F3.opExtrude","SWEPT_EDGE",EDGE,{"disambiguationData":[OSD([sQuery(id+"F2.wireOp",EDGE,"E42.top"),sQuery(id+"F2.wireOp",EDGE,"E42.left")])]});
            var Q13;
            Q13=makeQuery(id+"F3.opExtrude","SWEPT_EDGE",EDGE,{"disambiguationData":[OSD([sQuery(id+"F2.wireOp",EDGE,"E43.top"),sQuery(id+"F2.wireOp",EDGE,"E43.left")])]});
            var Q14;
            Q14=makeQuery(id+"F3.opExtrude","SWEPT_EDGE",EDGE,{"disambiguationData":[OSD([sQuery(id+"F2.wireOp",EDGE,"E43.bottom"),sQuery(id+"F2.wireOp",EDGE,"E43.left")])]});
            var Q15;
            Q15=makeQuery(id+"F3.opExtrude","SWEPT_EDGE",EDGE,{"disambiguationData":[OSD([sQuery(id+"F2.wireOp",EDGE,"E43.top"),sQuery(id+"F2.wireOp",EDGE,"E43.right")])]});
            var Q16;
            Q16=makeQuery(id+"F4.opExtrude","SWEPT_EDGE",EDGE,{"disambiguationData":[OSD([sQuery(id+"F1.wireOp",EDGE,"E24.bottom"),sQuery(id+"F1.wireOp",EDGE,"E24.right")])]});
            var Q17;
            Q17=makeQuery(id+"F4.opExtrude","SWEPT_EDGE",EDGE,{"disambiguationData":[OSD([sQuery(id+"F1.wireOp",EDGE,"E24.top"),sQuery(id+"F1.wireOp",EDGE,"E24.left")])]});
            var Q18;
            Q18=makeQuery(id+"F4.opExtrude","SWEPT_EDGE",EDGE,{"disambiguationData":[OSD([sQuery(id+"F1.wireOp",EDGE,"E24.top"),sQuery(id+"F1.wireOp",EDGE,"E24.right")])]});
            var Q19;
            Q19=makeQuery(id+"F4.opExtrude","SWEPT_EDGE",EDGE,{"disambiguationData":[OSD([sQuery(id+"F1.wireOp",EDGE,"E24.bottom"),sQuery(id+"F1.wireOp",EDGE,"E24.left")])]});
            var Q20;
            Q20=makeQuery(id+"F4.opExtrude","SWEPT_EDGE",EDGE,{"disambiguationData":[OSD([sQuery(id+"F1.wireOp",EDGE,"E25.bottom"),sQuery(id+"F1.wireOp",EDGE,"E25.right")])]});
            var Q21;
            Q21=makeQuery(id+"F4.opExtrude","SWEPT_EDGE",EDGE,{"disambiguationData":[OSD([sQuery(id+"F1.wireOp",EDGE,"E25.bottom"),sQuery(id+"F1.wireOp",EDGE,"E25.left")])]});
            var Q22;
            Q22=makeQuery(id+"F4.opExtrude","SWEPT_EDGE",EDGE,{"disambiguationData":[OSD([sQuery(id+"F1.wireOp",EDGE,"E25.top"),sQuery(id+"F1.wireOp",EDGE,"E25.left")])]});
            var Q23;
            Q23=makeQuery(id+"F4.opExtrude","SWEPT_EDGE",EDGE,{"disambiguationData":[OSD([sQuery(id+"F1.wireOp",EDGE,"E25.top"),sQuery(id+"F1.wireOp",EDGE,"E25.right")])]});
            chamfer(context, id + "F13", {"entities" : qUnion([Q0, Q1, Q2, Q3, Q4, Q5, Q6, Q7, Q8, Q9, Q10, Q11, Q12, Q13, Q14, Q15, Q16, Q17, Q18, Q19, Q20, Q21, Q22, Q23]), "width" : 1.6 * mm, "tangentPropagation" : true});
        }
        {
            var Q0;
            Q0=makeQuery(id+"F4.opExtrude","CAP_EDGE",EDGE,{"disambiguationData":[OSD([sQuery(id+"F1.wireOp",EDGE,"EttqwHYU-FuiR-qyt9-x16j-VCJwsENre23n")])],"isStart":false});
            var Q1;
            Q1=makeQuery(id+"F4.opExtrude","CAP_EDGE",EDGE,{"disambiguationData":[OSD([sQuery(id+"F1.wireOp",EDGE,"cyoMv6yO-WyV3-IXOB-3UQH-2AG7HBtNmJlT")])],"isStart":false});
            var Q2;
            Q2=makeQuery(id+"F4.opExtrude","CAP_EDGE",EDGE,{"disambiguationData":[OSD([sQuery(id+"F1.wireOp",EDGE,"cyoMv6yO-WyV3-IXOB-3UQH-2AG7HBtNmJlT")])],"isStart":true});
            var Q3;
            Q3=makeQuery(id+"F4.opExtrude","CAP_EDGE",EDGE,{"disambiguationData":[OSD([sQuery(id+"F1.wireOp",EDGE,"EttqwHYU-FuiR-qyt9-x16j-VCJwsENre23n")])],"isStart":true});
            var Q4;
            Q4=makeQuery(id+"F3.opExtrude","CAP_EDGE",EDGE,{"disambiguationData":[OSD([sQuery(id+"F2.wireOp",EDGE,"EmU0cS1E-6PPl-wBW3-uqTC-LOs51Vsq1UZG")])],"isStart":true});
            var Q5;
            Q5=makeQuery(id+"F3.opExtrude","CAP_EDGE",EDGE,{"disambiguationData":[OSD([sQuery(id+"F2.wireOp",EDGE,"EmU0cS1E-6PPl-wBW3-uqTC-LOs51Vsq1UZG")])],"isStart":false});
            var Q6;
            Q6=makeQuery(id+"F3.opExtrude","CAP_EDGE",EDGE,{"disambiguationData":[OSD([sQuery(id+"F2.wireOp",EDGE,"QTA5FS13-UDDy-iq4O-vZLj-EMgIGIXr1umF")])],"isStart":false});
            var Q7;
            Q7=makeQuery(id+"F3.opExtrude","CAP_EDGE",EDGE,{"disambiguationData":[OSD([sQuery(id+"F2.wireOp",EDGE,"QTA5FS13-UDDy-iq4O-vZLj-EMgIGIXr1umF")])],"isStart":true});
            var Q8;
            Q8=makeQuery(id+"F4.opExtrude","CAP_EDGE",EDGE,{"disambiguationData":[OSD([sQuery(id+"F1.wireOp",EDGE,"E13")])],"isStart":false});
            var Q9;
            Q9=makeQuery(id+"F4.opExtrude","CAP_EDGE",EDGE,{"disambiguationData":[OSD([sQuery(id+"F1.wireOp",EDGE,"E14")])],"isStart":false});
            var Q10;
            Q10=makeQuery(id+"F4.opExtrude","CAP_EDGE",EDGE,{"disambiguationData":[OSD([sQuery(id+"F1.wireOp",EDGE,"E14")])],"isStart":true});
            var Q11;
            Q11=makeQuery(id+"F4.opExtrude","CAP_EDGE",EDGE,{"disambiguationData":[OSD([sQuery(id+"F1.wireOp",EDGE,"E13")])],"isStart":true});
            var Q12;
            Q12=makeQuery(id+"F3.opExtrude","CAP_EDGE",EDGE,{"disambiguationData":[OSD([sQuery(id+"F2.wireOp",EDGE,"E44")])],"isStart":false});
            var Q13;
            Q13=makeQuery(id+"F3.opExtrude","CAP_EDGE",EDGE,{"disambiguationData":[OSD([sQuery(id+"F2.wireOp",EDGE,"E46")])],"isStart":true});
            var Q14;
            Q14=makeQuery(id+"F3.opExtrude","CAP_EDGE",EDGE,{"disambiguationData":[OSD([sQuery(id+"F2.wireOp",EDGE,"E44")])],"isStart":true});
            var Q15;
            Q15=makeQuery(id+"F3.opExtrude","CAP_EDGE",EDGE,{"disambiguationData":[OSD([sQuery(id+"F2.wireOp",EDGE,"E46")])],"isStart":false});
            chamfer(context, id + "F14", {"entities" : qUnion([Q0, Q1, Q2, Q3, Q4, Q5, Q6, Q7, Q8, Q9, Q10, Q11, Q12, Q13, Q14, Q15]), "width" : 1 * mm});
        }
        {
            var Q0;
            Q0=makeQuery(id+"F4.opExtrude","CAP_EDGE",EDGE,{"disambiguationData":[OSD([sQuery(id+"F1.wireOp",EDGE,"E15")])],"isStart":false});
            var Q1;
            Q1=makeQuery(id+"F4.opExtrude","SWEPT_EDGE",EDGE,{"disambiguationData":[OSD([sQuery(id+"F1.wireOp",EDGE,"E13"),sQuery(id+"F1.wireOp",EDGE,"E15")])]});
            var Q2;
            Q2=makeQuery(id+"F4.opExtrude","CAP_EDGE",EDGE,{"disambiguationData":[OSD([sQuery(id+"F1.wireOp",EDGE,"E15")])],"isStart":true});
            var Q3;
            Q3=makeQuery(id+"F4.opExtrude","SWEPT_EDGE",EDGE,{"disambiguationData":[OSD([sQuery(id+"F1.wireOp",EDGE,"E14"),sQuery(id+"F1.wireOp",EDGE,"E15")])]});
            var Q4;
            Q4=makeQuery(id+"F3.opExtrude","CAP_EDGE",EDGE,{"disambiguationData":[OSD([sQuery(id+"F2.wireOp",EDGE,"E45")])],"isStart":true});
            var Q5;
            Q5=makeQuery(id+"F3.opExtrude","SWEPT_EDGE",EDGE,{"disambiguationData":[OSD([sQuery(id+"F2.wireOp",EDGE,"E44"),sQuery(id+"F2.wireOp",EDGE,"E45")])]});
            var Q6;
            Q6=makeQuery(id+"F3.opExtrude","CAP_EDGE",EDGE,{"disambiguationData":[OSD([sQuery(id+"F2.wireOp",EDGE,"E45")])],"isStart":false});
            var Q7;
            Q7=makeQuery(id+"F3.opExtrude","SWEPT_EDGE",EDGE,{"disambiguationData":[OSD([sQuery(id+"F2.wireOp",EDGE,"E45"),sQuery(id+"F2.wireOp",EDGE,"E46")])]});
            chamfer(context, id + "F15", {"entities" : qUnion([Q0, Q1, Q2, Q3, Q4, Q5, Q6, Q7]), "width" : 1 * mm, "tangentPropagation" : true});
        }
        {
            var Q0;
            Q0=qCreatedBy(makeId("Top.planeOp"),FACE);
            cPlane(context, id + "F16", {"entities" : qUnion([Q0]), "cplaneType" : CPlaneType.OFFSET, "offset" : 15 * mm, "oppositeDirection" : true, "width" : 150 * mm, "height" : 150 * mm});
        }
        {
            var Q0;
            Q0=qCreatedBy(id+"F16.planeOp",FACE);
            var sketch = newSketch(context, id + "F17", { "sketchPlane" : qUnion([Q0])});
            skPoint(sketch, "E66.0", {"position": v(15.3, 4) * mm});
            skPoint(sketch, "E67.0", {"position": v(18.5, 4) * mm});
            skLineSegment(sketch, "E68.right", {"start": v(22.5, 4) * mm, "end": v(22.5, 3.6) * mm});
            skLineSegment(sketch, "E69", {"start": v(22.5, 3.6) * mm, "end": v(18.5, 3.6) * mm});
            skLineSegment(sketch, "E70", {"start": v(18.5, 3.6) * mm, "end": v(18.5, 4) * mm});
            skLineSegment(sketch, "E71", {"start": v(22.5, 4) * mm, "end": v(18.5, 4) * mm});
            skPoint(sketch, "E72.0", {"position": v(4, 18.5) * mm});
            skPoint(sketch, "E72.1", {"position": v(4, 16.9) * mm});
            skLineSegment(sketch, "E73.bottom", {"start": v(4, 18.5) * mm, "end": v(3.6, 18.5) * mm});
            skLineSegment(sketch, "E73.top", {"start": v(4, 22.5) * mm, "end": v(3.6, 22.5) * mm});
            skLineSegment(sketch, "E73.left", {"start": v(4, 18.5) * mm, "end": v(4, 22.5) * mm});
            skLineSegment(sketch, "E73.right", {"start": v(3.6, 18.5) * mm, "end": v(3.6, 22.5) * mm});
            skSolve(sketch);
        }
        {
            var Q0;
            Q0=makeQuery(id+"F17.imprint","IMPRINT",FACE,{"disambiguationData":[TD([[makeQuery(id+"F17.imprint","IMPRINT",EDGE,{"derivedFrom":sQuery(id+"F17.wireOp",EDGE,"E68.right")}),-1.0]])]});
            var Q1;
            Q1=makeQuery(id+"F4.opExtrude","CAP_EDGE",EDGE,{"disambiguationData":[OSD([sQuery(id+"F1.wireOp",EDGE,"E9.right")])],"isStart":true});
            var Q2;
            {var subQ0=sQuery(id+"F1.wireOp",EDGE,"E9.right");var subQ1=sQuery(id+"F1.wireOp",EDGE,"E9.bottom");Q2=makeQuery(id+"F12.opChamfer","BLEND_EDGE",EDGE,{"blendedFrom":[makeQuery(id+"F4.opExtrude","SWEPT_EDGE",EDGE,{"disambiguationData":[OSD([subQ1,subQ0])]}),makeQuery(id+"F4.opExtrude","CAP_FACE",FACE,{"disambiguationData":[OSD([sQuery(id+"F1.wireOp",EDGE,"E8.top"),sQuery(id+"F1.wireOp",EDGE,"E8.left"),sQuery(id+"F1.wireOp",EDGE,"E8.right"),subQ1,sQuery(id+"F1.wireOp",EDGE,"E9.top"),subQ0,sQuery(id+"F1.wireOp",EDGE,"E10.left"),sQuery(id+"F1.wireOp",EDGE,"E11.top"),sQuery(id+"F1.wireOp",EDGE,"E11.right"),sQuery(id+"F1.wireOp",EDGE,"E13"),sQuery(id+"F1.wireOp",EDGE,"E14"),sQuery(id+"F1.wireOp",EDGE,"E15"),sQuery(id+"F1.wireOp",EDGE,"E16"),sQuery(id+"F1.wireOp",EDGE,"E17"),sQuery(id+"F1.wireOp",EDGE,"E19"),sQuery(id+"F1.wireOp",EDGE,"E20"),sQuery(id+"F1.wireOp",EDGE,"E23.top"),sQuery(id+"F1.wireOp",EDGE,"E23.left"),sQuery(id+"F1.wireOp",EDGE,"E23.right"),sQuery(id+"F1.wireOp",EDGE,"E24.bottom"),sQuery(id+"F1.wireOp",EDGE,"E24.top"),sQuery(id+"F1.wireOp",EDGE,"E24.left"),sQuery(id+"F1.wireOp",EDGE,"E24.right"),sQuery(id+"F1.wireOp",EDGE,"E25.bottom"),sQuery(id+"F1.wireOp",EDGE,"E25.top"),sQuery(id+"F1.wireOp",EDGE,"E25.left"),sQuery(id+"F1.wireOp",EDGE,"E25.right")])],"isStart":true})],"blendedInto":[makeQuery(id+"F4.opExtrude","CAP_FACE",FACE,{"disambiguationData":[OSD([sQuery(id+"F1.wireOp",EDGE,"E8.top"),sQuery(id+"F1.wireOp",EDGE,"E8.left"),sQuery(id+"F1.wireOp",EDGE,"E8.right"),subQ1,sQuery(id+"F1.wireOp",EDGE,"E9.top"),subQ0,sQuery(id+"F1.wireOp",EDGE,"E10.left"),sQuery(id+"F1.wireOp",EDGE,"E11.top"),sQuery(id+"F1.wireOp",EDGE,"E11.right"),sQuery(id+"F1.wireOp",EDGE,"E13"),sQuery(id+"F1.wireOp",EDGE,"E14"),sQuery(id+"F1.wireOp",EDGE,"E15"),sQuery(id+"F1.wireOp",EDGE,"E16"),sQuery(id+"F1.wireOp",EDGE,"E17"),sQuery(id+"F1.wireOp",EDGE,"E19"),sQuery(id+"F1.wireOp",EDGE,"E20"),sQuery(id+"F1.wireOp",EDGE,"E23.top"),sQuery(id+"F1.wireOp",EDGE,"E23.left"),sQuery(id+"F1.wireOp",EDGE,"E23.right"),sQuery(id+"F1.wireOp",EDGE,"E24.bottom"),sQuery(id+"F1.wireOp",EDGE,"E24.top"),sQuery(id+"F1.wireOp",EDGE,"E24.left"),sQuery(id+"F1.wireOp",EDGE,"E24.right"),sQuery(id+"F1.wireOp",EDGE,"E25.bottom"),sQuery(id+"F1.wireOp",EDGE,"E25.top"),sQuery(id+"F1.wireOp",EDGE,"E25.left"),sQuery(id+"F1.wireOp",EDGE,"E25.right")])],"isStart":true})]});}
            var Q3;
            Q3=makeQuery(id+"F4.opExtrude","CAP_EDGE",EDGE,{"disambiguationData":[OSD([sQuery(id+"F1.wireOp",EDGE,"E9.bottom"),sQuery(id+"F1.wireOp",EDGE,"E16")])],"isStart":true});
            var Q4;
            {var subQ0=sQuery(id+"F1.wireOp",EDGE,"E14");Q4=makeQuery(id+"F14.opChamfer","BLEND_EDGE",EDGE,{"blendedFrom":[makeQuery(id+"F4.opExtrude","CAP_EDGE",EDGE,{"disambiguationData":[OSD([subQ0])],"isStart":true}),makeQuery(id+"F4.opExtrude","CAP_FACE",FACE,{"disambiguationData":[OSD([sQuery(id+"F1.wireOp",EDGE,"E8.top"),sQuery(id+"F1.wireOp",EDGE,"E8.left"),sQuery(id+"F1.wireOp",EDGE,"E8.right"),sQuery(id+"F1.wireOp",EDGE,"E9.bottom"),sQuery(id+"F1.wireOp",EDGE,"E9.top"),sQuery(id+"F1.wireOp",EDGE,"E9.right"),sQuery(id+"F1.wireOp",EDGE,"E10.left"),sQuery(id+"F1.wireOp",EDGE,"E11.top"),sQuery(id+"F1.wireOp",EDGE,"E11.right"),sQuery(id+"F1.wireOp",EDGE,"E13"),subQ0,sQuery(id+"F1.wireOp",EDGE,"E15"),sQuery(id+"F1.wireOp",EDGE,"E16"),sQuery(id+"F1.wireOp",EDGE,"E17"),sQuery(id+"F1.wireOp",EDGE,"E19"),sQuery(id+"F1.wireOp",EDGE,"E20"),sQuery(id+"F1.wireOp",EDGE,"E23.top"),sQuery(id+"F1.wireOp",EDGE,"E23.left"),sQuery(id+"F1.wireOp",EDGE,"E23.right"),sQuery(id+"F1.wireOp",EDGE,"E24.bottom"),sQuery(id+"F1.wireOp",EDGE,"E24.top"),sQuery(id+"F1.wireOp",EDGE,"E24.left"),sQuery(id+"F1.wireOp",EDGE,"E24.right"),sQuery(id+"F1.wireOp",EDGE,"E25.bottom"),sQuery(id+"F1.wireOp",EDGE,"E25.top"),sQuery(id+"F1.wireOp",EDGE,"E25.left"),sQuery(id+"F1.wireOp",EDGE,"E25.right")])],"isStart":true})],"blendedInto":[makeQuery(id+"F4.opExtrude","CAP_FACE",FACE,{"disambiguationData":[OSD([sQuery(id+"F1.wireOp",EDGE,"E8.top"),sQuery(id+"F1.wireOp",EDGE,"E8.left"),sQuery(id+"F1.wireOp",EDGE,"E8.right"),sQuery(id+"F1.wireOp",EDGE,"E9.bottom"),sQuery(id+"F1.wireOp",EDGE,"E9.top"),sQuery(id+"F1.wireOp",EDGE,"E9.right"),sQuery(id+"F1.wireOp",EDGE,"E10.left"),sQuery(id+"F1.wireOp",EDGE,"E11.top"),sQuery(id+"F1.wireOp",EDGE,"E11.right"),sQuery(id+"F1.wireOp",EDGE,"E13"),subQ0,sQuery(id+"F1.wireOp",EDGE,"E15"),sQuery(id+"F1.wireOp",EDGE,"E16"),sQuery(id+"F1.wireOp",EDGE,"E17"),sQuery(id+"F1.wireOp",EDGE,"E19"),sQuery(id+"F1.wireOp",EDGE,"E20"),sQuery(id+"F1.wireOp",EDGE,"E23.top"),sQuery(id+"F1.wireOp",EDGE,"E23.left"),sQuery(id+"F1.wireOp",EDGE,"E23.right"),sQuery(id+"F1.wireOp",EDGE,"E24.bottom"),sQuery(id+"F1.wireOp",EDGE,"E24.top"),sQuery(id+"F1.wireOp",EDGE,"E24.left"),sQuery(id+"F1.wireOp",EDGE,"E24.right"),sQuery(id+"F1.wireOp",EDGE,"E25.bottom"),sQuery(id+"F1.wireOp",EDGE,"E25.top"),sQuery(id+"F1.wireOp",EDGE,"E25.left"),sQuery(id+"F1.wireOp",EDGE,"E25.right")])],"isStart":true})]});}
            var Q5;
            Q5=makeQuery(id+"F4.opExtrude","CAP_EDGE",EDGE,{"disambiguationData":[OSD([sQuery(id+"F1.wireOp",EDGE,"E15")])],"isStart":true});
            var Q6;
            {var subQ0=sQuery(id+"F1.wireOp",EDGE,"E13");Q6=makeQuery(id+"F14.opChamfer","BLEND_EDGE",EDGE,{"blendedFrom":[makeQuery(id+"F4.opExtrude","CAP_EDGE",EDGE,{"disambiguationData":[OSD([subQ0])],"isStart":true}),makeQuery(id+"F4.opExtrude","CAP_FACE",FACE,{"disambiguationData":[OSD([sQuery(id+"F1.wireOp",EDGE,"E8.top"),sQuery(id+"F1.wireOp",EDGE,"E8.left"),sQuery(id+"F1.wireOp",EDGE,"E8.right"),sQuery(id+"F1.wireOp",EDGE,"E9.bottom"),sQuery(id+"F1.wireOp",EDGE,"E9.top"),sQuery(id+"F1.wireOp",EDGE,"E9.right"),sQuery(id+"F1.wireOp",EDGE,"E10.left"),sQuery(id+"F1.wireOp",EDGE,"E11.top"),sQuery(id+"F1.wireOp",EDGE,"E11.right"),subQ0,sQuery(id+"F1.wireOp",EDGE,"E14"),sQuery(id+"F1.wireOp",EDGE,"E15"),sQuery(id+"F1.wireOp",EDGE,"E16"),sQuery(id+"F1.wireOp",EDGE,"E17"),sQuery(id+"F1.wireOp",EDGE,"E19"),sQuery(id+"F1.wireOp",EDGE,"E20"),sQuery(id+"F1.wireOp",EDGE,"E23.top"),sQuery(id+"F1.wireOp",EDGE,"E23.left"),sQuery(id+"F1.wireOp",EDGE,"E23.right"),sQuery(id+"F1.wireOp",EDGE,"E24.bottom"),sQuery(id+"F1.wireOp",EDGE,"E24.top"),sQuery(id+"F1.wireOp",EDGE,"E24.left"),sQuery(id+"F1.wireOp",EDGE,"E24.right"),sQuery(id+"F1.wireOp",EDGE,"E25.bottom"),sQuery(id+"F1.wireOp",EDGE,"E25.top"),sQuery(id+"F1.wireOp",EDGE,"E25.left"),sQuery(id+"F1.wireOp",EDGE,"E25.right")])],"isStart":true})],"blendedInto":[makeQuery(id+"F4.opExtrude","CAP_FACE",FACE,{"disambiguationData":[OSD([sQuery(id+"F1.wireOp",EDGE,"E8.top"),sQuery(id+"F1.wireOp",EDGE,"E8.left"),sQuery(id+"F1.wireOp",EDGE,"E8.right"),sQuery(id+"F1.wireOp",EDGE,"E9.bottom"),sQuery(id+"F1.wireOp",EDGE,"E9.top"),sQuery(id+"F1.wireOp",EDGE,"E9.right"),sQuery(id+"F1.wireOp",EDGE,"E10.left"),sQuery(id+"F1.wireOp",EDGE,"E11.top"),sQuery(id+"F1.wireOp",EDGE,"E11.right"),subQ0,sQuery(id+"F1.wireOp",EDGE,"E14"),sQuery(id+"F1.wireOp",EDGE,"E15"),sQuery(id+"F1.wireOp",EDGE,"E16"),sQuery(id+"F1.wireOp",EDGE,"E17"),sQuery(id+"F1.wireOp",EDGE,"E19"),sQuery(id+"F1.wireOp",EDGE,"E20"),sQuery(id+"F1.wireOp",EDGE,"E23.top"),sQuery(id+"F1.wireOp",EDGE,"E23.left"),sQuery(id+"F1.wireOp",EDGE,"E23.right"),sQuery(id+"F1.wireOp",EDGE,"E24.bottom"),sQuery(id+"F1.wireOp",EDGE,"E24.top"),sQuery(id+"F1.wireOp",EDGE,"E24.left"),sQuery(id+"F1.wireOp",EDGE,"E24.right"),sQuery(id+"F1.wireOp",EDGE,"E25.bottom"),sQuery(id+"F1.wireOp",EDGE,"E25.top"),sQuery(id+"F1.wireOp",EDGE,"E25.left"),sQuery(id+"F1.wireOp",EDGE,"E25.right")])],"isStart":true})]});}
            var Q7;
            Q7=makeQuery(id+"F4.opExtrude","CAP_EDGE",EDGE,{"disambiguationData":[OSD([sQuery(id+"F1.wireOp",EDGE,"E8.left"),sQuery(id+"F1.wireOp",EDGE,"E10.left"),sQuery(id+"F1.wireOp",EDGE,"E17")])],"isStart":true});
            var Q8;
            Q8=makeQuery(id+"F4.opExtrude","CAP_EDGE",EDGE,{"disambiguationData":[OSD([sQuery(id+"F1.wireOp",EDGE,"E8.top")])],"isStart":true});
            var Q9;
            Q9=makeQuery(id+"F4.opExtrude","CAP_EDGE",EDGE,{"disambiguationData":[OSD([sQuery(id+"F1.wireOp",EDGE,"E8.right")])],"isStart":true});
            var Q10;
            Q10=makeQuery(id+"F4.opExtrude","CAP_EDGE",EDGE,{"disambiguationData":[OSD([sQuery(id+"F1.wireOp",EDGE,"E11.top")])],"isStart":true});
            var Q11;
            Q11=makeQuery(id+"F4.opExtrude","CAP_EDGE",EDGE,{"disambiguationData":[OSD([sQuery(id+"F1.wireOp",EDGE,"E11.right")])],"isStart":true});
            var Q12;
            {var subQ0=sQuery(id+"F1.wireOp",EDGE,"E9.right");var subQ1=sQuery(id+"F1.wireOp",EDGE,"E9.top");Q12=makeQuery(id+"F12.opChamfer","BLEND_EDGE",EDGE,{"blendedFrom":[makeQuery(id+"F4.opExtrude","SWEPT_EDGE",EDGE,{"disambiguationData":[OSD([subQ1,subQ0])]}),makeQuery(id+"F4.opExtrude","CAP_FACE",FACE,{"disambiguationData":[OSD([sQuery(id+"F1.wireOp",EDGE,"E8.top"),sQuery(id+"F1.wireOp",EDGE,"E8.left"),sQuery(id+"F1.wireOp",EDGE,"E8.right"),sQuery(id+"F1.wireOp",EDGE,"E9.bottom"),subQ1,subQ0,sQuery(id+"F1.wireOp",EDGE,"E10.left"),sQuery(id+"F1.wireOp",EDGE,"E11.top"),sQuery(id+"F1.wireOp",EDGE,"E11.right"),sQuery(id+"F1.wireOp",EDGE,"E13"),sQuery(id+"F1.wireOp",EDGE,"E14"),sQuery(id+"F1.wireOp",EDGE,"E15"),sQuery(id+"F1.wireOp",EDGE,"E16"),sQuery(id+"F1.wireOp",EDGE,"E17"),sQuery(id+"F1.wireOp",EDGE,"E19"),sQuery(id+"F1.wireOp",EDGE,"E20"),sQuery(id+"F1.wireOp",EDGE,"E23.top"),sQuery(id+"F1.wireOp",EDGE,"E23.left"),sQuery(id+"F1.wireOp",EDGE,"E23.right"),sQuery(id+"F1.wireOp",EDGE,"E24.bottom"),sQuery(id+"F1.wireOp",EDGE,"E24.top"),sQuery(id+"F1.wireOp",EDGE,"E24.left"),sQuery(id+"F1.wireOp",EDGE,"E24.right"),sQuery(id+"F1.wireOp",EDGE,"E25.bottom"),sQuery(id+"F1.wireOp",EDGE,"E25.top"),sQuery(id+"F1.wireOp",EDGE,"E25.left"),sQuery(id+"F1.wireOp",EDGE,"E25.right")])],"isStart":true})],"blendedInto":[makeQuery(id+"F4.opExtrude","CAP_FACE",FACE,{"disambiguationData":[OSD([sQuery(id+"F1.wireOp",EDGE,"E8.top"),sQuery(id+"F1.wireOp",EDGE,"E8.left"),sQuery(id+"F1.wireOp",EDGE,"E8.right"),sQuery(id+"F1.wireOp",EDGE,"E9.bottom"),subQ1,subQ0,sQuery(id+"F1.wireOp",EDGE,"E10.left"),sQuery(id+"F1.wireOp",EDGE,"E11.top"),sQuery(id+"F1.wireOp",EDGE,"E11.right"),sQuery(id+"F1.wireOp",EDGE,"E13"),sQuery(id+"F1.wireOp",EDGE,"E14"),sQuery(id+"F1.wireOp",EDGE,"E15"),sQuery(id+"F1.wireOp",EDGE,"E16"),sQuery(id+"F1.wireOp",EDGE,"E17"),sQuery(id+"F1.wireOp",EDGE,"E19"),sQuery(id+"F1.wireOp",EDGE,"E20"),sQuery(id+"F1.wireOp",EDGE,"E23.top"),sQuery(id+"F1.wireOp",EDGE,"E23.left"),sQuery(id+"F1.wireOp",EDGE,"E23.right"),sQuery(id+"F1.wireOp",EDGE,"E24.bottom"),sQuery(id+"F1.wireOp",EDGE,"E24.top"),sQuery(id+"F1.wireOp",EDGE,"E24.left"),sQuery(id+"F1.wireOp",EDGE,"E24.right"),sQuery(id+"F1.wireOp",EDGE,"E25.bottom"),sQuery(id+"F1.wireOp",EDGE,"E25.top"),sQuery(id+"F1.wireOp",EDGE,"E25.left"),sQuery(id+"F1.wireOp",EDGE,"E25.right")])],"isStart":true})]});}
            var Q13;
            Q13=makeQuery(id+"F4.opExtrude","CAP_EDGE",EDGE,{"disambiguationData":[OSD([sQuery(id+"F1.wireOp",EDGE,"E9.top")])],"isStart":true});
            var Q14;
            {var subQ0=sQuery(id+"F1.wireOp",EDGE,"E15");Q14=makeQuery(id+"F15.opChamfer","BLEND_EDGE",EDGE,{"blendedFrom":[makeQuery(id+"F4.opExtrude","CAP_EDGE",EDGE,{"disambiguationData":[OSD([subQ0])],"isStart":true}),makeQuery(id+"F4.opExtrude","CAP_FACE",FACE,{"disambiguationData":[OSD([sQuery(id+"F1.wireOp",EDGE,"E8.top"),sQuery(id+"F1.wireOp",EDGE,"E8.left"),sQuery(id+"F1.wireOp",EDGE,"E8.right"),sQuery(id+"F1.wireOp",EDGE,"E9.bottom"),sQuery(id+"F1.wireOp",EDGE,"E9.top"),sQuery(id+"F1.wireOp",EDGE,"E9.right"),sQuery(id+"F1.wireOp",EDGE,"E10.left"),sQuery(id+"F1.wireOp",EDGE,"E11.top"),sQuery(id+"F1.wireOp",EDGE,"E11.right"),sQuery(id+"F1.wireOp",EDGE,"E13"),sQuery(id+"F1.wireOp",EDGE,"E14"),subQ0,sQuery(id+"F1.wireOp",EDGE,"E16"),sQuery(id+"F1.wireOp",EDGE,"E17"),sQuery(id+"F1.wireOp",EDGE,"E19"),sQuery(id+"F1.wireOp",EDGE,"E20"),sQuery(id+"F1.wireOp",EDGE,"E23.top"),sQuery(id+"F1.wireOp",EDGE,"E23.left"),sQuery(id+"F1.wireOp",EDGE,"E23.right"),sQuery(id+"F1.wireOp",EDGE,"E24.bottom"),sQuery(id+"F1.wireOp",EDGE,"E24.top"),sQuery(id+"F1.wireOp",EDGE,"E24.left"),sQuery(id+"F1.wireOp",EDGE,"E24.right"),sQuery(id+"F1.wireOp",EDGE,"E25.bottom"),sQuery(id+"F1.wireOp",EDGE,"E25.top"),sQuery(id+"F1.wireOp",EDGE,"E25.left"),sQuery(id+"F1.wireOp",EDGE,"E25.right")])],"isStart":true})],"blendedInto":[makeQuery(id+"F4.opExtrude","CAP_FACE",FACE,{"disambiguationData":[OSD([sQuery(id+"F1.wireOp",EDGE,"E8.top"),sQuery(id+"F1.wireOp",EDGE,"E8.left"),sQuery(id+"F1.wireOp",EDGE,"E8.right"),sQuery(id+"F1.wireOp",EDGE,"E9.bottom"),sQuery(id+"F1.wireOp",EDGE,"E9.top"),sQuery(id+"F1.wireOp",EDGE,"E9.right"),sQuery(id+"F1.wireOp",EDGE,"E10.left"),sQuery(id+"F1.wireOp",EDGE,"E11.top"),sQuery(id+"F1.wireOp",EDGE,"E11.right"),sQuery(id+"F1.wireOp",EDGE,"E13"),sQuery(id+"F1.wireOp",EDGE,"E14"),subQ0,sQuery(id+"F1.wireOp",EDGE,"E16"),sQuery(id+"F1.wireOp",EDGE,"E17"),sQuery(id+"F1.wireOp",EDGE,"E19"),sQuery(id+"F1.wireOp",EDGE,"E20"),sQuery(id+"F1.wireOp",EDGE,"E23.top"),sQuery(id+"F1.wireOp",EDGE,"E23.left"),sQuery(id+"F1.wireOp",EDGE,"E23.right"),sQuery(id+"F1.wireOp",EDGE,"E24.bottom"),sQuery(id+"F1.wireOp",EDGE,"E24.top"),sQuery(id+"F1.wireOp",EDGE,"E24.left"),sQuery(id+"F1.wireOp",EDGE,"E24.right"),sQuery(id+"F1.wireOp",EDGE,"E25.bottom"),sQuery(id+"F1.wireOp",EDGE,"E25.top"),sQuery(id+"F1.wireOp",EDGE,"E25.left"),sQuery(id+"F1.wireOp",EDGE,"E25.right")])],"isStart":true})]});}
            var Q15;
            {var subQ0=sQuery(id+"F1.wireOp",EDGE,"E17");var subQ1=sQuery(id+"F1.wireOp",EDGE,"E13");Q15=makeQuery(id+"F11.opChamfer","BLEND_EDGE",EDGE,{"blendedFrom":[makeQuery(id+"F4.opExtrude","SWEPT_EDGE",EDGE,{"disambiguationData":[OSD([subQ1,subQ0])]}),makeQuery(id+"F4.opExtrude","CAP_FACE",FACE,{"disambiguationData":[OSD([sQuery(id+"F1.wireOp",EDGE,"E8.top"),sQuery(id+"F1.wireOp",EDGE,"E8.right"),sQuery(id+"F1.wireOp",EDGE,"E9.bottom"),sQuery(id+"F1.wireOp",EDGE,"E9.top"),sQuery(id+"F1.wireOp",EDGE,"E9.right"),sQuery(id+"F1.wireOp",EDGE,"E10.left"),sQuery(id+"F1.wireOp",EDGE,"E11.top"),sQuery(id+"F1.wireOp",EDGE,"E11.right"),subQ1,sQuery(id+"F1.wireOp",EDGE,"E14"),sQuery(id+"F1.wireOp",EDGE,"E15"),sQuery(id+"F1.wireOp",EDGE,"E16"),subQ0,sQuery(id+"F1.wireOp",EDGE,"E19"),sQuery(id+"F1.wireOp",EDGE,"E20"),sQuery(id+"F1.wireOp",EDGE,"E23.top"),sQuery(id+"F1.wireOp",EDGE,"E23.left"),sQuery(id+"F1.wireOp",EDGE,"E23.right"),sQuery(id+"F1.wireOp",EDGE,"E24.bottom"),sQuery(id+"F1.wireOp",EDGE,"E24.top"),sQuery(id+"F1.wireOp",EDGE,"E24.left"),sQuery(id+"F1.wireOp",EDGE,"E24.right"),sQuery(id+"F1.wireOp",EDGE,"E25.bottom"),sQuery(id+"F1.wireOp",EDGE,"E25.top"),sQuery(id+"F1.wireOp",EDGE,"E25.left"),sQuery(id+"F1.wireOp",EDGE,"E25.right")])],"isStart":true})],"blendedInto":[makeQuery(id+"F4.opExtrude","CAP_FACE",FACE,{"disambiguationData":[OSD([sQuery(id+"F1.wireOp",EDGE,"E8.top"),sQuery(id+"F1.wireOp",EDGE,"E8.right"),sQuery(id+"F1.wireOp",EDGE,"E9.bottom"),sQuery(id+"F1.wireOp",EDGE,"E9.top"),sQuery(id+"F1.wireOp",EDGE,"E9.right"),sQuery(id+"F1.wireOp",EDGE,"E10.left"),sQuery(id+"F1.wireOp",EDGE,"E11.top"),sQuery(id+"F1.wireOp",EDGE,"E11.right"),subQ1,sQuery(id+"F1.wireOp",EDGE,"E14"),sQuery(id+"F1.wireOp",EDGE,"E15"),sQuery(id+"F1.wireOp",EDGE,"E16"),subQ0,sQuery(id+"F1.wireOp",EDGE,"E19"),sQuery(id+"F1.wireOp",EDGE,"E20"),sQuery(id+"F1.wireOp",EDGE,"E23.top"),sQuery(id+"F1.wireOp",EDGE,"E23.left"),sQuery(id+"F1.wireOp",EDGE,"E23.right"),sQuery(id+"F1.wireOp",EDGE,"E24.bottom"),sQuery(id+"F1.wireOp",EDGE,"E24.top"),sQuery(id+"F1.wireOp",EDGE,"E24.left"),sQuery(id+"F1.wireOp",EDGE,"E24.right"),sQuery(id+"F1.wireOp",EDGE,"E25.bottom"),sQuery(id+"F1.wireOp",EDGE,"E25.top"),sQuery(id+"F1.wireOp",EDGE,"E25.left"),sQuery(id+"F1.wireOp",EDGE,"E25.right")])],"isStart":true})]});}
            sweep(context, id + "F18", {"operationType" : NewBodyOperationType.ADD, "profiles" : qUnion([Q0]), "path" : qUnion([Q1, Q2, Q3, Q4, Q5, Q6, Q7, Q8, Q9, Q10, Q11, Q12, Q13, Q14, Q15])});
        }
        {
            var Q0;
            Q0=makeQuery(id+"F17.imprint","IMPRINT",FACE,{"disambiguationData":[TD([[makeQuery(id+"F17.imprint","IMPRINT",EDGE,{"derivedFrom":sQuery(id+"F17.wireOp",EDGE,"E73.bottom")}),-1.0]])]});
            var Q1;
            Q1=makeQuery(id+"F3.opExtrude","CAP_EDGE",EDGE,{"disambiguationData":[OSD([sQuery(id+"F2.wireOp",EDGE,"E32.right")])],"isStart":false});
            var Q2;
            {var subQ0=sQuery(id+"F2.wireOp",EDGE,"E32.right");var subQ1=sQuery(id+"F2.wireOp",EDGE,"E32.bottom");Q2=makeQuery(id+"F12.opChamfer","BLEND_EDGE",EDGE,{"blendedFrom":[makeQuery(id+"F3.opExtrude","SWEPT_EDGE",EDGE,{"disambiguationData":[OSD([subQ1,subQ0])]}),makeQuery(id+"F3.opExtrude","CAP_FACE",FACE,{"disambiguationData":[OSD([sQuery(id+"F2.wireOp",EDGE,"E31.top"),sQuery(id+"F2.wireOp",EDGE,"E31.left"),sQuery(id+"F2.wireOp",EDGE,"E31.right"),subQ1,sQuery(id+"F2.wireOp",EDGE,"E32.top"),subQ0,sQuery(id+"F2.wireOp",EDGE,"E33.left"),sQuery(id+"F2.wireOp",EDGE,"E34.top"),sQuery(id+"F2.wireOp",EDGE,"E34.right"),sQuery(id+"F2.wireOp",EDGE,"E36.top"),sQuery(id+"F2.wireOp",EDGE,"E36.left"),sQuery(id+"F2.wireOp",EDGE,"E36.right"),sQuery(id+"F2.wireOp",EDGE,"E37"),sQuery(id+"F2.wireOp",EDGE,"E40"),sQuery(id+"F2.wireOp",EDGE,"E42.bottom"),sQuery(id+"F2.wireOp",EDGE,"E42.top"),sQuery(id+"F2.wireOp",EDGE,"E42.left"),sQuery(id+"F2.wireOp",EDGE,"E42.right"),sQuery(id+"F2.wireOp",EDGE,"E43.bottom"),sQuery(id+"F2.wireOp",EDGE,"E43.top"),sQuery(id+"F2.wireOp",EDGE,"E43.left"),sQuery(id+"F2.wireOp",EDGE,"E43.right"),sQuery(id+"F2.wireOp",EDGE,"E44"),sQuery(id+"F2.wireOp",EDGE,"E45"),sQuery(id+"F2.wireOp",EDGE,"E46"),sQuery(id+"F2.wireOp",EDGE,"E47"),sQuery(id+"F2.wireOp",EDGE,"E48")])],"isStart":false})],"blendedInto":[makeQuery(id+"F3.opExtrude","CAP_FACE",FACE,{"disambiguationData":[OSD([sQuery(id+"F2.wireOp",EDGE,"E31.top"),sQuery(id+"F2.wireOp",EDGE,"E31.left"),sQuery(id+"F2.wireOp",EDGE,"E31.right"),subQ1,sQuery(id+"F2.wireOp",EDGE,"E32.top"),subQ0,sQuery(id+"F2.wireOp",EDGE,"E33.left"),sQuery(id+"F2.wireOp",EDGE,"E34.top"),sQuery(id+"F2.wireOp",EDGE,"E34.right"),sQuery(id+"F2.wireOp",EDGE,"E36.top"),sQuery(id+"F2.wireOp",EDGE,"E36.left"),sQuery(id+"F2.wireOp",EDGE,"E36.right"),sQuery(id+"F2.wireOp",EDGE,"E37"),sQuery(id+"F2.wireOp",EDGE,"E40"),sQuery(id+"F2.wireOp",EDGE,"E42.bottom"),sQuery(id+"F2.wireOp",EDGE,"E42.top"),sQuery(id+"F2.wireOp",EDGE,"E42.left"),sQuery(id+"F2.wireOp",EDGE,"E42.right"),sQuery(id+"F2.wireOp",EDGE,"E43.bottom"),sQuery(id+"F2.wireOp",EDGE,"E43.top"),sQuery(id+"F2.wireOp",EDGE,"E43.left"),sQuery(id+"F2.wireOp",EDGE,"E43.right"),sQuery(id+"F2.wireOp",EDGE,"E44"),sQuery(id+"F2.wireOp",EDGE,"E45"),sQuery(id+"F2.wireOp",EDGE,"E46"),sQuery(id+"F2.wireOp",EDGE,"E47"),sQuery(id+"F2.wireOp",EDGE,"E48")])],"isStart":false})]});}
            var Q3;
            Q3=makeQuery(id+"F3.opExtrude","CAP_EDGE",EDGE,{"disambiguationData":[OSD([sQuery(id+"F2.wireOp",EDGE,"E32.bottom"),sQuery(id+"F2.wireOp",EDGE,"E37")])],"isStart":false});
            var Q4;
            Q4=makeQuery(id+"F3.opExtrude","CAP_EDGE",EDGE,{"disambiguationData":[OSD([sQuery(id+"F2.wireOp",EDGE,"E34.top")])],"isStart":false});
            var Q5;
            Q5=makeQuery(id+"F3.opExtrude","CAP_EDGE",EDGE,{"disambiguationData":[OSD([sQuery(id+"F2.wireOp",EDGE,"E34.right")])],"isStart":false});
            var Q6;
            Q6=makeQuery(id+"F3.opExtrude","CAP_EDGE",EDGE,{"disambiguationData":[OSD([sQuery(id+"F2.wireOp",EDGE,"E31.top")])],"isStart":false});
            var Q7;
            Q7=makeQuery(id+"F3.opExtrude","CAP_EDGE",EDGE,{"disambiguationData":[OSD([sQuery(id+"F2.wireOp",EDGE,"E31.left")])],"isStart":false});
            var Q8;
            Q8=makeQuery(id+"F3.opExtrude","CAP_EDGE",EDGE,{"disambiguationData":[OSD([sQuery(id+"F2.wireOp",EDGE,"E31.right"),sQuery(id+"F2.wireOp",EDGE,"E33.left"),sQuery(id+"F2.wireOp",EDGE,"E48")])],"isStart":false});
            var Q9;
            {var subQ0=sQuery(id+"F2.wireOp",EDGE,"E44");Q9=makeQuery(id+"F14.opChamfer","BLEND_EDGE",EDGE,{"blendedFrom":[makeQuery(id+"F3.opExtrude","CAP_EDGE",EDGE,{"disambiguationData":[OSD([subQ0])],"isStart":false}),makeQuery(id+"F3.opExtrude","CAP_FACE",FACE,{"disambiguationData":[OSD([sQuery(id+"F2.wireOp",EDGE,"E31.top"),sQuery(id+"F2.wireOp",EDGE,"E31.left"),sQuery(id+"F2.wireOp",EDGE,"E31.right"),sQuery(id+"F2.wireOp",EDGE,"E32.bottom"),sQuery(id+"F2.wireOp",EDGE,"E32.top"),sQuery(id+"F2.wireOp",EDGE,"E32.right"),sQuery(id+"F2.wireOp",EDGE,"E33.left"),sQuery(id+"F2.wireOp",EDGE,"E34.top"),sQuery(id+"F2.wireOp",EDGE,"E34.right"),sQuery(id+"F2.wireOp",EDGE,"E36.top"),sQuery(id+"F2.wireOp",EDGE,"E36.left"),sQuery(id+"F2.wireOp",EDGE,"E36.right"),sQuery(id+"F2.wireOp",EDGE,"E37"),sQuery(id+"F2.wireOp",EDGE,"E40"),sQuery(id+"F2.wireOp",EDGE,"E42.bottom"),sQuery(id+"F2.wireOp",EDGE,"E42.top"),sQuery(id+"F2.wireOp",EDGE,"E42.left"),sQuery(id+"F2.wireOp",EDGE,"E42.right"),sQuery(id+"F2.wireOp",EDGE,"E43.bottom"),sQuery(id+"F2.wireOp",EDGE,"E43.top"),sQuery(id+"F2.wireOp",EDGE,"E43.left"),sQuery(id+"F2.wireOp",EDGE,"E43.right"),subQ0,sQuery(id+"F2.wireOp",EDGE,"E45"),sQuery(id+"F2.wireOp",EDGE,"E46"),sQuery(id+"F2.wireOp",EDGE,"E47"),sQuery(id+"F2.wireOp",EDGE,"E48")])],"isStart":false})],"blendedInto":[makeQuery(id+"F3.opExtrude","CAP_FACE",FACE,{"disambiguationData":[OSD([sQuery(id+"F2.wireOp",EDGE,"E31.top"),sQuery(id+"F2.wireOp",EDGE,"E31.left"),sQuery(id+"F2.wireOp",EDGE,"E31.right"),sQuery(id+"F2.wireOp",EDGE,"E32.bottom"),sQuery(id+"F2.wireOp",EDGE,"E32.top"),sQuery(id+"F2.wireOp",EDGE,"E32.right"),sQuery(id+"F2.wireOp",EDGE,"E33.left"),sQuery(id+"F2.wireOp",EDGE,"E34.top"),sQuery(id+"F2.wireOp",EDGE,"E34.right"),sQuery(id+"F2.wireOp",EDGE,"E36.top"),sQuery(id+"F2.wireOp",EDGE,"E36.left"),sQuery(id+"F2.wireOp",EDGE,"E36.right"),sQuery(id+"F2.wireOp",EDGE,"E37"),sQuery(id+"F2.wireOp",EDGE,"E40"),sQuery(id+"F2.wireOp",EDGE,"E42.bottom"),sQuery(id+"F2.wireOp",EDGE,"E42.top"),sQuery(id+"F2.wireOp",EDGE,"E42.left"),sQuery(id+"F2.wireOp",EDGE,"E42.right"),sQuery(id+"F2.wireOp",EDGE,"E43.bottom"),sQuery(id+"F2.wireOp",EDGE,"E43.top"),sQuery(id+"F2.wireOp",EDGE,"E43.left"),sQuery(id+"F2.wireOp",EDGE,"E43.right"),subQ0,sQuery(id+"F2.wireOp",EDGE,"E45"),sQuery(id+"F2.wireOp",EDGE,"E46"),sQuery(id+"F2.wireOp",EDGE,"E47"),sQuery(id+"F2.wireOp",EDGE,"E48")])],"isStart":false})]});}
            var Q10;
            Q10=makeQuery(id+"F3.opExtrude","CAP_EDGE",EDGE,{"disambiguationData":[OSD([sQuery(id+"F2.wireOp",EDGE,"E45")])],"isStart":false});
            var Q11;
            {var subQ0=sQuery(id+"F2.wireOp",EDGE,"E46");Q11=makeQuery(id+"F14.opChamfer","BLEND_EDGE",EDGE,{"blendedFrom":[makeQuery(id+"F3.opExtrude","CAP_EDGE",EDGE,{"disambiguationData":[OSD([subQ0])],"isStart":false}),makeQuery(id+"F3.opExtrude","CAP_FACE",FACE,{"disambiguationData":[OSD([sQuery(id+"F2.wireOp",EDGE,"E31.top"),sQuery(id+"F2.wireOp",EDGE,"E31.left"),sQuery(id+"F2.wireOp",EDGE,"E31.right"),sQuery(id+"F2.wireOp",EDGE,"E32.bottom"),sQuery(id+"F2.wireOp",EDGE,"E32.top"),sQuery(id+"F2.wireOp",EDGE,"E32.right"),sQuery(id+"F2.wireOp",EDGE,"E33.left"),sQuery(id+"F2.wireOp",EDGE,"E34.top"),sQuery(id+"F2.wireOp",EDGE,"E34.right"),sQuery(id+"F2.wireOp",EDGE,"E36.top"),sQuery(id+"F2.wireOp",EDGE,"E36.left"),sQuery(id+"F2.wireOp",EDGE,"E36.right"),sQuery(id+"F2.wireOp",EDGE,"E37"),sQuery(id+"F2.wireOp",EDGE,"E40"),sQuery(id+"F2.wireOp",EDGE,"E42.bottom"),sQuery(id+"F2.wireOp",EDGE,"E42.top"),sQuery(id+"F2.wireOp",EDGE,"E42.left"),sQuery(id+"F2.wireOp",EDGE,"E42.right"),sQuery(id+"F2.wireOp",EDGE,"E43.bottom"),sQuery(id+"F2.wireOp",EDGE,"E43.top"),sQuery(id+"F2.wireOp",EDGE,"E43.left"),sQuery(id+"F2.wireOp",EDGE,"E43.right"),sQuery(id+"F2.wireOp",EDGE,"E44"),sQuery(id+"F2.wireOp",EDGE,"E45"),subQ0,sQuery(id+"F2.wireOp",EDGE,"E47"),sQuery(id+"F2.wireOp",EDGE,"E48")])],"isStart":false})],"blendedInto":[makeQuery(id+"F3.opExtrude","CAP_FACE",FACE,{"disambiguationData":[OSD([sQuery(id+"F2.wireOp",EDGE,"E31.top"),sQuery(id+"F2.wireOp",EDGE,"E31.left"),sQuery(id+"F2.wireOp",EDGE,"E31.right"),sQuery(id+"F2.wireOp",EDGE,"E32.bottom"),sQuery(id+"F2.wireOp",EDGE,"E32.top"),sQuery(id+"F2.wireOp",EDGE,"E32.right"),sQuery(id+"F2.wireOp",EDGE,"E33.left"),sQuery(id+"F2.wireOp",EDGE,"E34.top"),sQuery(id+"F2.wireOp",EDGE,"E34.right"),sQuery(id+"F2.wireOp",EDGE,"E36.top"),sQuery(id+"F2.wireOp",EDGE,"E36.left"),sQuery(id+"F2.wireOp",EDGE,"E36.right"),sQuery(id+"F2.wireOp",EDGE,"E37"),sQuery(id+"F2.wireOp",EDGE,"E40"),sQuery(id+"F2.wireOp",EDGE,"E42.bottom"),sQuery(id+"F2.wireOp",EDGE,"E42.top"),sQuery(id+"F2.wireOp",EDGE,"E42.left"),sQuery(id+"F2.wireOp",EDGE,"E42.right"),sQuery(id+"F2.wireOp",EDGE,"E43.bottom"),sQuery(id+"F2.wireOp",EDGE,"E43.top"),sQuery(id+"F2.wireOp",EDGE,"E43.left"),sQuery(id+"F2.wireOp",EDGE,"E43.right"),sQuery(id+"F2.wireOp",EDGE,"E44"),sQuery(id+"F2.wireOp",EDGE,"E45"),subQ0,sQuery(id+"F2.wireOp",EDGE,"E47"),sQuery(id+"F2.wireOp",EDGE,"E48")])],"isStart":false})]});}
            var Q12;
            {var subQ0=sQuery(id+"F2.wireOp",EDGE,"E32.right");var subQ1=sQuery(id+"F2.wireOp",EDGE,"E32.top");Q12=makeQuery(id+"F12.opChamfer","BLEND_EDGE",EDGE,{"blendedFrom":[makeQuery(id+"F3.opExtrude","SWEPT_EDGE",EDGE,{"disambiguationData":[OSD([subQ1,subQ0])]}),makeQuery(id+"F3.opExtrude","CAP_FACE",FACE,{"disambiguationData":[OSD([sQuery(id+"F2.wireOp",EDGE,"E31.top"),sQuery(id+"F2.wireOp",EDGE,"E31.left"),sQuery(id+"F2.wireOp",EDGE,"E31.right"),sQuery(id+"F2.wireOp",EDGE,"E32.bottom"),subQ1,subQ0,sQuery(id+"F2.wireOp",EDGE,"E33.left"),sQuery(id+"F2.wireOp",EDGE,"E34.top"),sQuery(id+"F2.wireOp",EDGE,"E34.right"),sQuery(id+"F2.wireOp",EDGE,"E36.top"),sQuery(id+"F2.wireOp",EDGE,"E36.left"),sQuery(id+"F2.wireOp",EDGE,"E36.right"),sQuery(id+"F2.wireOp",EDGE,"E37"),sQuery(id+"F2.wireOp",EDGE,"E40"),sQuery(id+"F2.wireOp",EDGE,"E42.bottom"),sQuery(id+"F2.wireOp",EDGE,"E42.top"),sQuery(id+"F2.wireOp",EDGE,"E42.left"),sQuery(id+"F2.wireOp",EDGE,"E42.right"),sQuery(id+"F2.wireOp",EDGE,"E43.bottom"),sQuery(id+"F2.wireOp",EDGE,"E43.top"),sQuery(id+"F2.wireOp",EDGE,"E43.left"),sQuery(id+"F2.wireOp",EDGE,"E43.right"),sQuery(id+"F2.wireOp",EDGE,"E44"),sQuery(id+"F2.wireOp",EDGE,"E45"),sQuery(id+"F2.wireOp",EDGE,"E46"),sQuery(id+"F2.wireOp",EDGE,"E47"),sQuery(id+"F2.wireOp",EDGE,"E48")])],"isStart":false})],"blendedInto":[makeQuery(id+"F3.opExtrude","CAP_FACE",FACE,{"disambiguationData":[OSD([sQuery(id+"F2.wireOp",EDGE,"E31.top"),sQuery(id+"F2.wireOp",EDGE,"E31.left"),sQuery(id+"F2.wireOp",EDGE,"E31.right"),sQuery(id+"F2.wireOp",EDGE,"E32.bottom"),subQ1,subQ0,sQuery(id+"F2.wireOp",EDGE,"E33.left"),sQuery(id+"F2.wireOp",EDGE,"E34.top"),sQuery(id+"F2.wireOp",EDGE,"E34.right"),sQuery(id+"F2.wireOp",EDGE,"E36.top"),sQuery(id+"F2.wireOp",EDGE,"E36.left"),sQuery(id+"F2.wireOp",EDGE,"E36.right"),sQuery(id+"F2.wireOp",EDGE,"E37"),sQuery(id+"F2.wireOp",EDGE,"E40"),sQuery(id+"F2.wireOp",EDGE,"E42.bottom"),sQuery(id+"F2.wireOp",EDGE,"E42.top"),sQuery(id+"F2.wireOp",EDGE,"E42.left"),sQuery(id+"F2.wireOp",EDGE,"E42.right"),sQuery(id+"F2.wireOp",EDGE,"E43.bottom"),sQuery(id+"F2.wireOp",EDGE,"E43.top"),sQuery(id+"F2.wireOp",EDGE,"E43.left"),sQuery(id+"F2.wireOp",EDGE,"E43.right"),sQuery(id+"F2.wireOp",EDGE,"E44"),sQuery(id+"F2.wireOp",EDGE,"E45"),sQuery(id+"F2.wireOp",EDGE,"E46"),sQuery(id+"F2.wireOp",EDGE,"E47"),sQuery(id+"F2.wireOp",EDGE,"E48")])],"isStart":false})]});}
            var Q13;
            Q13=makeQuery(id+"F3.opExtrude","CAP_EDGE",EDGE,{"disambiguationData":[OSD([sQuery(id+"F2.wireOp",EDGE,"E32.top")])],"isStart":false});
            var Q14;
            {var subQ0=sQuery(id+"F2.wireOp",EDGE,"E45");Q14=makeQuery(id+"F15.opChamfer","BLEND_EDGE",EDGE,{"blendedFrom":[makeQuery(id+"F3.opExtrude","CAP_EDGE",EDGE,{"disambiguationData":[OSD([subQ0])],"isStart":false}),makeQuery(id+"F3.opExtrude","CAP_FACE",FACE,{"disambiguationData":[OSD([sQuery(id+"F2.wireOp",EDGE,"E31.top"),sQuery(id+"F2.wireOp",EDGE,"E31.left"),sQuery(id+"F2.wireOp",EDGE,"E31.right"),sQuery(id+"F2.wireOp",EDGE,"E32.bottom"),sQuery(id+"F2.wireOp",EDGE,"E32.top"),sQuery(id+"F2.wireOp",EDGE,"E32.right"),sQuery(id+"F2.wireOp",EDGE,"E33.left"),sQuery(id+"F2.wireOp",EDGE,"E34.top"),sQuery(id+"F2.wireOp",EDGE,"E34.right"),sQuery(id+"F2.wireOp",EDGE,"E36.top"),sQuery(id+"F2.wireOp",EDGE,"E36.left"),sQuery(id+"F2.wireOp",EDGE,"E36.right"),sQuery(id+"F2.wireOp",EDGE,"E37"),sQuery(id+"F2.wireOp",EDGE,"E40"),sQuery(id+"F2.wireOp",EDGE,"E42.bottom"),sQuery(id+"F2.wireOp",EDGE,"E42.top"),sQuery(id+"F2.wireOp",EDGE,"E42.left"),sQuery(id+"F2.wireOp",EDGE,"E42.right"),sQuery(id+"F2.wireOp",EDGE,"E43.bottom"),sQuery(id+"F2.wireOp",EDGE,"E43.top"),sQuery(id+"F2.wireOp",EDGE,"E43.left"),sQuery(id+"F2.wireOp",EDGE,"E43.right"),sQuery(id+"F2.wireOp",EDGE,"E44"),subQ0,sQuery(id+"F2.wireOp",EDGE,"E46"),sQuery(id+"F2.wireOp",EDGE,"E47"),sQuery(id+"F2.wireOp",EDGE,"E48")])],"isStart":false})],"blendedInto":[makeQuery(id+"F3.opExtrude","CAP_FACE",FACE,{"disambiguationData":[OSD([sQuery(id+"F2.wireOp",EDGE,"E31.top"),sQuery(id+"F2.wireOp",EDGE,"E31.left"),sQuery(id+"F2.wireOp",EDGE,"E31.right"),sQuery(id+"F2.wireOp",EDGE,"E32.bottom"),sQuery(id+"F2.wireOp",EDGE,"E32.top"),sQuery(id+"F2.wireOp",EDGE,"E32.right"),sQuery(id+"F2.wireOp",EDGE,"E33.left"),sQuery(id+"F2.wireOp",EDGE,"E34.top"),sQuery(id+"F2.wireOp",EDGE,"E34.right"),sQuery(id+"F2.wireOp",EDGE,"E36.top"),sQuery(id+"F2.wireOp",EDGE,"E36.left"),sQuery(id+"F2.wireOp",EDGE,"E36.right"),sQuery(id+"F2.wireOp",EDGE,"E37"),sQuery(id+"F2.wireOp",EDGE,"E40"),sQuery(id+"F2.wireOp",EDGE,"E42.bottom"),sQuery(id+"F2.wireOp",EDGE,"E42.top"),sQuery(id+"F2.wireOp",EDGE,"E42.left"),sQuery(id+"F2.wireOp",EDGE,"E42.right"),sQuery(id+"F2.wireOp",EDGE,"E43.bottom"),sQuery(id+"F2.wireOp",EDGE,"E43.top"),sQuery(id+"F2.wireOp",EDGE,"E43.left"),sQuery(id+"F2.wireOp",EDGE,"E43.right"),sQuery(id+"F2.wireOp",EDGE,"E44"),subQ0,sQuery(id+"F2.wireOp",EDGE,"E46"),sQuery(id+"F2.wireOp",EDGE,"E47"),sQuery(id+"F2.wireOp",EDGE,"E48")])],"isStart":false})]});}
            var Q15;
            {var subQ0=sQuery(id+"F2.wireOp",EDGE,"E48");var subQ1=sQuery(id+"F2.wireOp",EDGE,"E44");Q15=makeQuery(id+"F11.opChamfer","BLEND_EDGE",EDGE,{"blendedFrom":[makeQuery(id+"F3.opExtrude","SWEPT_EDGE",EDGE,{"disambiguationData":[OSD([subQ1,subQ0])]}),makeQuery(id+"F3.opExtrude","CAP_FACE",FACE,{"disambiguationData":[OSD([sQuery(id+"F2.wireOp",EDGE,"E31.top"),sQuery(id+"F2.wireOp",EDGE,"E31.left"),sQuery(id+"F2.wireOp",EDGE,"E32.bottom"),sQuery(id+"F2.wireOp",EDGE,"E32.top"),sQuery(id+"F2.wireOp",EDGE,"E32.right"),sQuery(id+"F2.wireOp",EDGE,"E33.left"),sQuery(id+"F2.wireOp",EDGE,"E34.top"),sQuery(id+"F2.wireOp",EDGE,"E34.right"),sQuery(id+"F2.wireOp",EDGE,"E36.top"),sQuery(id+"F2.wireOp",EDGE,"E36.left"),sQuery(id+"F2.wireOp",EDGE,"E36.right"),sQuery(id+"F2.wireOp",EDGE,"E37"),sQuery(id+"F2.wireOp",EDGE,"E40"),sQuery(id+"F2.wireOp",EDGE,"E42.bottom"),sQuery(id+"F2.wireOp",EDGE,"E42.top"),sQuery(id+"F2.wireOp",EDGE,"E42.left"),sQuery(id+"F2.wireOp",EDGE,"E42.right"),sQuery(id+"F2.wireOp",EDGE,"E43.bottom"),sQuery(id+"F2.wireOp",EDGE,"E43.top"),sQuery(id+"F2.wireOp",EDGE,"E43.left"),sQuery(id+"F2.wireOp",EDGE,"E43.right"),subQ1,sQuery(id+"F2.wireOp",EDGE,"E45"),sQuery(id+"F2.wireOp",EDGE,"E46"),sQuery(id+"F2.wireOp",EDGE,"E47"),subQ0])],"isStart":false})],"blendedInto":[makeQuery(id+"F3.opExtrude","CAP_FACE",FACE,{"disambiguationData":[OSD([sQuery(id+"F2.wireOp",EDGE,"E31.top"),sQuery(id+"F2.wireOp",EDGE,"E31.left"),sQuery(id+"F2.wireOp",EDGE,"E32.bottom"),sQuery(id+"F2.wireOp",EDGE,"E32.top"),sQuery(id+"F2.wireOp",EDGE,"E32.right"),sQuery(id+"F2.wireOp",EDGE,"E33.left"),sQuery(id+"F2.wireOp",EDGE,"E34.top"),sQuery(id+"F2.wireOp",EDGE,"E34.right"),sQuery(id+"F2.wireOp",EDGE,"E36.top"),sQuery(id+"F2.wireOp",EDGE,"E36.left"),sQuery(id+"F2.wireOp",EDGE,"E36.right"),sQuery(id+"F2.wireOp",EDGE,"E37"),sQuery(id+"F2.wireOp",EDGE,"E40"),sQuery(id+"F2.wireOp",EDGE,"E42.bottom"),sQuery(id+"F2.wireOp",EDGE,"E42.top"),sQuery(id+"F2.wireOp",EDGE,"E42.left"),sQuery(id+"F2.wireOp",EDGE,"E42.right"),sQuery(id+"F2.wireOp",EDGE,"E43.bottom"),sQuery(id+"F2.wireOp",EDGE,"E43.top"),sQuery(id+"F2.wireOp",EDGE,"E43.left"),sQuery(id+"F2.wireOp",EDGE,"E43.right"),subQ1,sQuery(id+"F2.wireOp",EDGE,"E45"),sQuery(id+"F2.wireOp",EDGE,"E46"),sQuery(id+"F2.wireOp",EDGE,"E47"),subQ0])],"isStart":false})]});}
            sweep(context, id + "F19", {"operationType" : NewBodyOperationType.ADD, "profiles" : qUnion([Q0]), "path" : qUnion([Q1, Q2, Q3, Q4, Q5, Q6, Q7, Q8, Q9, Q10, Q11, Q12, Q13, Q14, Q15])});
        }
    });
